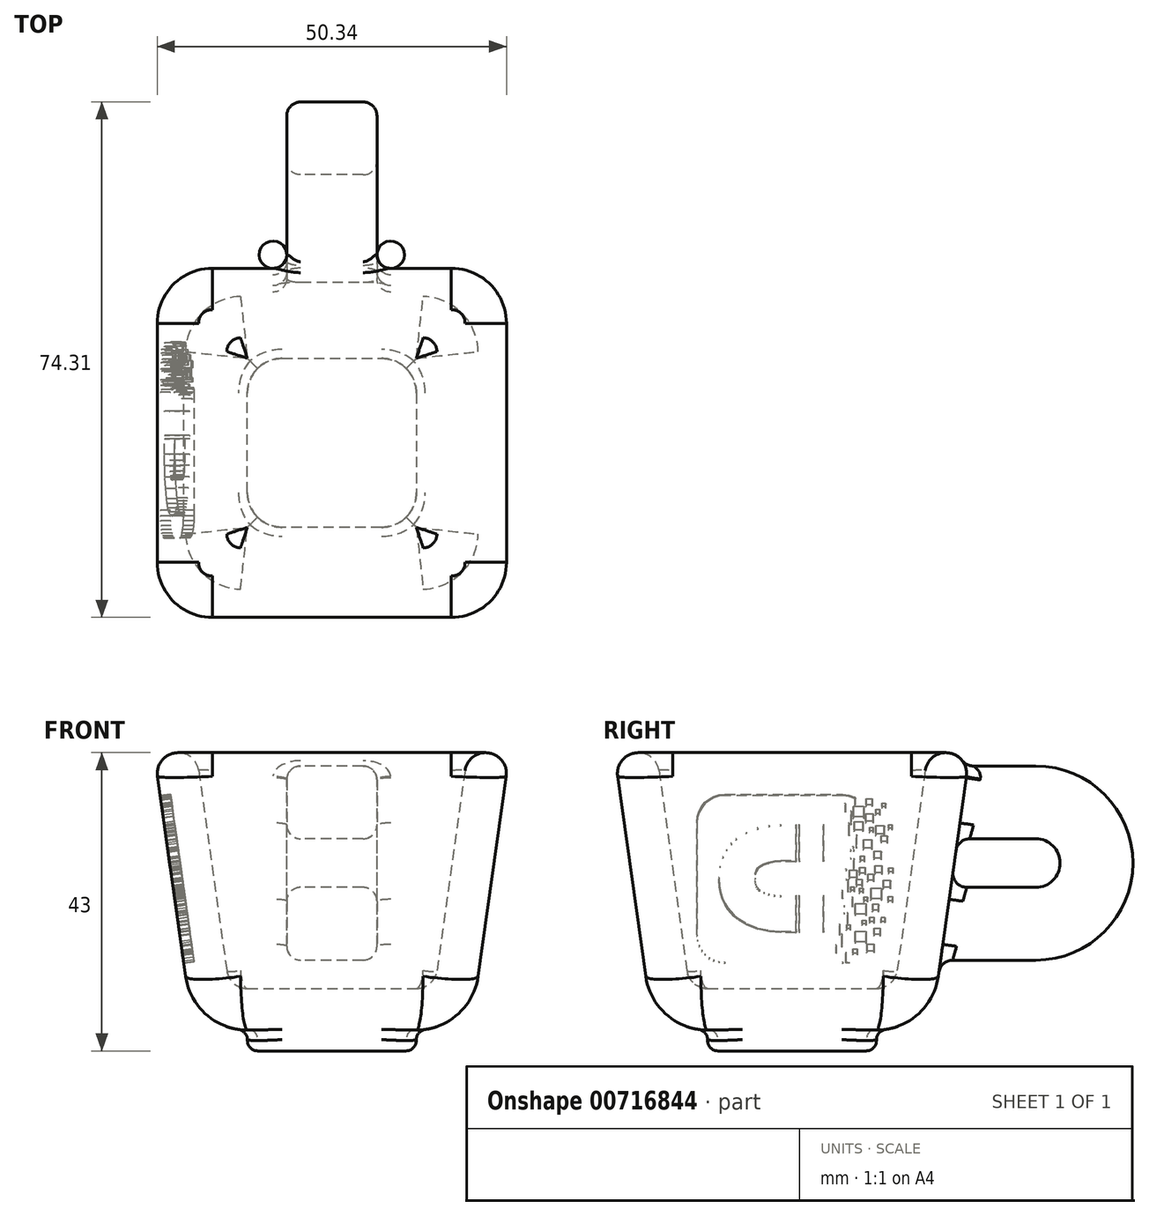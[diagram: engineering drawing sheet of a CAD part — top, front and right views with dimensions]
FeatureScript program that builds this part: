
annotation { "Feature Type Name" : "Feature", "Feature Type Description" : "" }
export const myFeature = defineFeature(function(context is Context, id is Id, definition is map)
    precondition{}
    {
        {
            var Q0;
            Q0=qCreatedBy(makeId("Top.planeOp"),FACE);
            var sketch = newSketch(context, id + "F0", { "sketchPlane" : qUnion([Q0])});
            skLineSegment(sketch, "E0.bottom", {"start": v(20, 20) * mm, "end": v(-20, 20) * mm});
            skLineSegment(sketch, "E0.top", {"start": v(20, -20) * mm, "end": v(-20, -20) * mm});
            skLineSegment(sketch, "E0.left", {"start": v(20, 20) * mm, "end": v(20, -20) * mm});
            skLineSegment(sketch, "E0.right", {"start": v(-20, 20) * mm, "end": v(-20, -20) * mm});
            skSolve(sketch);
        }
        {
            var Q0;
            Q0=makeQuery(id+"F0.imprint","IMPRINT",FACE,{"disambiguationData":[TD([[makeQuery(id+"F0.imprint","IMPRINT",EDGE,{"derivedFrom":sQuery(id+"F0.wireOp",EDGE,"E0.bottom")}),1.0]])]});
            extrude(context, id + "F1", {"entities" : qUnion([Q0]), "depth" : 40 * mm, "offsetDistance" : 25 * mm, "hasDraft" : true, "draftAngle" : 8 * degree});
        }
        {
            var Q0;
            Q0=makeQuery(id+"F1.opExtrude","SWEPT_EDGE",EDGE,{"disambiguationData":[OSD([sQuery(id+"F0.wireOp",EDGE,"E0.top"),sQuery(id+"F0.wireOp",EDGE,"E0.left")])]});
            var Q1;
            Q1=makeQuery(id+"F1.opExtrude","SWEPT_EDGE",EDGE,{"disambiguationData":[OSD([sQuery(id+"F0.wireOp",EDGE,"E0.top"),sQuery(id+"F0.wireOp",EDGE,"E0.right")])]});
            var Q2;
            Q2=makeQuery(id+"F1.opExtrude","SWEPT_EDGE",EDGE,{"disambiguationData":[OSD([sQuery(id+"F0.wireOp",EDGE,"E0.bottom"),sQuery(id+"F0.wireOp",EDGE,"E0.left")])]});
            var Q3;
            Q3=makeQuery(id+"F1.opExtrude","SWEPT_EDGE",EDGE,{"disambiguationData":[OSD([sQuery(id+"F0.wireOp",EDGE,"E0.bottom"),sQuery(id+"F0.wireOp",EDGE,"E0.right")])]});
            fillet(context, id + "F2", {"entities" : qUnion([Q0, Q1, Q2, Q3]), "radius" : 8 * mm, "tangentPropagation" : true, "allowEdgeOverflow" : false});
        }
        {
            var Q0;
            {var subQ0=sQuery(id+"F0.wireOp",EDGE,"E0.right");var subQ1=sQuery(id+"F0.wireOp",EDGE,"E0.bottom");Q0=makeQuery(id+"F2.opFillet","BLEND_EDGE",EDGE,{"blendedFrom":[makeQuery(id+"F1.opExtrude","SWEPT_EDGE",EDGE,{"disambiguationData":[OSD([subQ1,subQ0])]}),makeQuery(id+"F1.opExtrude","CAP_FACE",FACE,{"disambiguationData":[OSD([subQ1,sQuery(id+"F0.wireOp",EDGE,"E0.top"),sQuery(id+"F0.wireOp",EDGE,"E0.left"),subQ0])],"isStart":true})],"blendedInto":[makeQuery(id+"F1.opExtrude","CAP_FACE",FACE,{"disambiguationData":[OSD([subQ1,sQuery(id+"F0.wireOp",EDGE,"E0.top"),sQuery(id+"F0.wireOp",EDGE,"E0.left"),subQ0])],"isStart":true})]});}
            fillet(context, id + "F3", {"entities" : qUnion([Q0]), "radius" : 9 * mm, "tangentPropagation" : true, "allowEdgeOverflow" : false});
        }
        {
            var Q0;
            Q0=makeQuery(id+"F1.opExtrude","CAP_FACE",FACE,{"disambiguationData":[OSD([sQuery(id+"F0.wireOp",EDGE,"E0.bottom"),sQuery(id+"F0.wireOp",EDGE,"E0.top"),sQuery(id+"F0.wireOp",EDGE,"E0.left"),sQuery(id+"F0.wireOp",EDGE,"E0.right")])],"isStart":false});
            shell(context, id + "F4", {"entities" : qUnion([Q0]), "thickness" : 6 * mm});
        }
        {
            var Q0;
            {var subQ0=sQuery(id+"F0.wireOp",EDGE,"E0.left");Q0=makeQuery(id+"F4.opShell","OFFSET_EDGE",EDGE,{"disambiguationData":[OSD([subQ0]),TDD([makeQuery(id+"F1.opExtrude","CAP_EDGE",EDGE,{"disambiguationData":[OSD([subQ0])],"isStart":false})])]});}
            var Q1;
            {var subQ0=sQuery(id+"F0.wireOp",EDGE,"E0.left");var subQ1=sQuery(id+"F0.wireOp",EDGE,"E0.bottom");Q1=makeQuery(id+"F2.opFillet","BLEND_EDGE",EDGE,{"blendedFrom":[makeQuery(id+"F1.opExtrude","SWEPT_EDGE",EDGE,{"disambiguationData":[OSD([subQ1,subQ0])]}),makeQuery(id+"F1.opExtrude","CAP_FACE",FACE,{"disambiguationData":[OSD([subQ1,sQuery(id+"F0.wireOp",EDGE,"E0.top"),subQ0,sQuery(id+"F0.wireOp",EDGE,"E0.right")])],"isStart":false})],"blendedInto":[makeQuery(id+"F1.opExtrude","CAP_FACE",FACE,{"disambiguationData":[OSD([subQ1,sQuery(id+"F0.wireOp",EDGE,"E0.top"),subQ0,sQuery(id+"F0.wireOp",EDGE,"E0.right")])],"isStart":false})]});}
            fillet(context, id + "F5", {"entities" : qUnion([Q0, Q1]), "radius" : 3 * mm, "tangentPropagation" : true, "allowEdgeOverflow" : false});
        }
        {
            var Q0;
            Q0=qCreatedBy(makeId("Right.planeOp"),FACE);
            var sketch = newSketch(context, id + "F6", { "sketchPlane" : qUnion([Q0])});
            skArc(sketch, "E1", {"start": v(35.14, 20.58) * mm, "mid": v(38.64, 24.08) * mm, "end": v(35.14, 27.58) * mm});
            skLineSegment(sketch, "E2", {"start": v(35.14, 20.58) * mm, "end": v(20.07, 20.58) * mm});
            skLineSegment(sketch, "E3", {"start": v(35.14, 27.58) * mm, "end": v(20.46, 27.58) * mm});
            skLineSegment(sketch, "E4", {"start": v(35.14, 38.08) * mm, "end": v(21.04, 38.08) * mm});
            skLineSegment(sketch, "E5", {"start": v(35.14, 10.08) * mm, "end": v(18.28, 10.08) * mm});
            skLineSegment(sketch, "E6", {"start": v(18.28, 10.08) * mm, "end": v(20, 19.31) * mm});
            skLineSegment(sketch, "E7", {"start": v(20, 19.31) * mm, "end": v(20.07, 20.58) * mm});
            skLineSegment(sketch, "E8.trimOffspring", {"start": v(20.46, 27.58) * mm, "end": v(21.04, 38.08) * mm});
            skArc(sketch, "E9.trimOffspring", {"start": v(35.14, 10.08) * mm, "mid": v(49.14, 24.08) * mm, "end": v(35.14, 38.08) * mm});
            skPoint(sketch, "E10.0.start.orphan", {"position": v(25.14, 36.58) * mm});
            skPoint(sketch, "E11.trimOffspring.end.orphan", {"position": v(21.09, 7.75) * mm});
            skSolve(sketch);
        }
        {
            var Q0;
            Q0=makeQuery(id+"F6.imprint","IMPRINT",FACE,{"disambiguationData":[TD([[makeQuery(id+"F6.imprint","IMPRINT",EDGE,{"derivedFrom":sQuery(id+"F6.wireOp",EDGE,"E1")}),-1.0]])]});
            extrude(context, id + "F7", {"entities" : qUnion([Q0]), "operationType" : NewBodyOperationType.ADD, "depth" : 13 * mm, "offsetDistance" : 25 * mm, "symmetric" : true});
        }
        {
            var Q0;
            Q0=makeQuery(id+"F7.opExtrude","CAP_EDGE",EDGE,{"disambiguationData":[OSD([sQuery(id+"F6.wireOp",EDGE,"E9.trimOffspring")])],"isStart":false});
            var Q1;
            Q1=makeQuery(id+"F7.opExtrude","CAP_EDGE",EDGE,{"disambiguationData":[OSD([sQuery(id+"F6.wireOp",EDGE,"E3")])],"isStart":false});
            var Q2;
            Q2=makeQuery(id+"F7.opExtrude","CAP_EDGE",EDGE,{"disambiguationData":[OSD([sQuery(id+"F6.wireOp",EDGE,"E9.trimOffspring")])],"isStart":true});
            var Q3;
            Q3=makeQuery(id+"F7.opExtrude","CAP_EDGE",EDGE,{"disambiguationData":[OSD([sQuery(id+"F6.wireOp",EDGE,"E2")])],"isStart":true});
            fillet(context, id + "F8", {"entities" : qUnion([Q0, Q1, Q2, Q3]), "radius" : 2 * mm, "tangentPropagation" : true, "allowEdgeOverflow" : false});
        }
        {
            var Q0;
            Q0=makeQuery(id+"F8.opFillet","BLEND_EDGE",EDGE,{"blendedFrom":[makeQuery(id+"F7.opExtrude","CAP_EDGE",EDGE,{"disambiguationData":[OSD([sQuery(id+"F6.wireOp",EDGE,"E4")])],"isStart":true}),makeQuery(id+"F5.opFillet","BLEND_FACE",FACE,{"disambiguationData":[OSD([sQuery(id+"F0.wireOp",EDGE,"E0.bottom")])]})],"blendedInto":[makeQuery(id+"F5.opFillet","BLEND_FACE",FACE,{"disambiguationData":[OSD([sQuery(id+"F0.wireOp",EDGE,"E0.bottom")])]})]});
            var Q1;
            Q1=makeQuery(id+"F8.opFillet","BLEND_EDGE",EDGE,{"blendedFrom":[makeQuery(id+"F7.opExtrude","CAP_EDGE",EDGE,{"disambiguationData":[OSD([sQuery(id+"F6.wireOp",EDGE,"E2")])],"isStart":true}),makeQuery(id+"F1.opExtrude","SWEPT_FACE",FACE,{"disambiguationData":[OSD([sQuery(id+"F0.wireOp",EDGE,"E0.bottom")])]})],"blendedInto":[makeQuery(id+"F1.opExtrude","SWEPT_FACE",FACE,{"disambiguationData":[OSD([sQuery(id+"F0.wireOp",EDGE,"E0.bottom")])]})]});
            fillet(context, id + "F9", {"entities" : qUnion([Q0, Q1]), "radius" : 2 * mm, "tangentPropagation" : true, "allowEdgeOverflow" : false});
        }
        {
            var Q0;
            Q0=makeQuery(id+"F1.opExtrude","SWEPT_FACE",FACE,{"disambiguationData":[OSD([sQuery(id+"F0.wireOp",EDGE,"E0.right")])]});
            var sketch = newSketch(context, id + "F10", { "sketchPlane" : qUnion([Q0])});
            skLineSegment(sketch, "E12", {"start": v(-12.87, 18.96) * mm, "end": v(-12.87, 18.44) * mm});
            skLineSegment(sketch, "E13", {"start": v(-12.87, 18.44) * mm, "end": v(-13.38, 18.44) * mm});
            skLineSegment(sketch, "E14", {"start": v(-13.38, 18.44) * mm, "end": v(-13.38, 18.96) * mm});
            skLineSegment(sketch, "E15", {"start": v(-13.38, 18.96) * mm, "end": v(-12.87, 18.96) * mm});
            skLineSegment(sketch, "E16", {"start": v(-8.79, 13.79) * mm, "end": v(-8.79, 14.4) * mm});
            skLineSegment(sketch, "E17", {"start": v(-8.79, 14.4) * mm, "end": v(-9.4, 14.4) * mm});
            skLineSegment(sketch, "E18", {"start": v(-9.4, 14.4) * mm, "end": v(-9.4, 13.79) * mm});
            skLineSegment(sketch, "E19", {"start": v(-9.4, 13.79) * mm, "end": v(-8.79, 13.79) * mm});
            skLineSegment(sketch, "E20", {"start": v(-10.8, 14.1) * mm, "end": v(-10.8, 15.13) * mm});
            skLineSegment(sketch, "E21", {"start": v(-10.8, 15.13) * mm, "end": v(-11.83, 15.13) * mm});
            skLineSegment(sketch, "E22", {"start": v(-11.83, 15.13) * mm, "end": v(-11.83, 14.1) * mm});
            skLineSegment(sketch, "E23", {"start": v(-11.83, 14.1) * mm, "end": v(-10.8, 14.1) * mm});
            skLineSegment(sketch, "E24", {"start": v(-10.14, 18.04) * mm, "end": v(-10.14, 18.56) * mm});
            skLineSegment(sketch, "E25", {"start": v(-10.14, 18.56) * mm, "end": v(-10.65, 18.56) * mm});
            skLineSegment(sketch, "E26", {"start": v(-10.65, 18.56) * mm, "end": v(-10.65, 18.04) * mm});
            skLineSegment(sketch, "E27", {"start": v(-10.65, 18.04) * mm, "end": v(-10.14, 18.04) * mm});
            skLineSegment(sketch, "E28", {"start": v(-9.1, 15.4) * mm, "end": v(-9.1, 16.95) * mm});
            skLineSegment(sketch, "E29", {"start": v(-9.1, 16.95) * mm, "end": v(-10.65, 16.95) * mm});
            skLineSegment(sketch, "E30", {"start": v(-10.65, 16.95) * mm, "end": v(-10.65, 15.4) * mm});
            skLineSegment(sketch, "E31", {"start": v(-10.65, 15.4) * mm, "end": v(-9.1, 15.4) * mm});
            skLineSegment(sketch, "E32", {"start": v(-9.1, 19.44) * mm, "end": v(-9.1, 20.99) * mm});
            skLineSegment(sketch, "E33", {"start": v(-9.1, 20.99) * mm, "end": v(-10.65, 20.99) * mm});
            skLineSegment(sketch, "E34", {"start": v(-10.65, 20.99) * mm, "end": v(-10.65, 19.44) * mm});
            skLineSegment(sketch, "E35", {"start": v(-10.65, 19.44) * mm, "end": v(-9.1, 19.44) * mm});
            skLineSegment(sketch, "E36", {"start": v(-11.83, 16.5) * mm, "end": v(-11.83, 17.38) * mm});
            skLineSegment(sketch, "E37", {"start": v(-11.83, 17.38) * mm, "end": v(-12.72, 17.38) * mm});
            skLineSegment(sketch, "E38", {"start": v(-12.72, 17.38) * mm, "end": v(-12.72, 16.5) * mm});
            skLineSegment(sketch, "E39", {"start": v(-12.72, 16.5) * mm, "end": v(-11.83, 16.5) * mm});
            skLineSegment(sketch, "E40", {"start": v(-11.6, 20.02) * mm, "end": v(-11.6, 20.9) * mm});
            skLineSegment(sketch, "E41", {"start": v(-11.6, 20.9) * mm, "end": v(-12.48, 20.9) * mm});
            skLineSegment(sketch, "E42", {"start": v(-12.48, 20.9) * mm, "end": v(-12.48, 20.02) * mm});
            skLineSegment(sketch, "E43", {"start": v(-12.48, 20.02) * mm, "end": v(-11.6, 20.02) * mm});
            skLineSegment(sketch, "E44", {"start": v(-8.46, 23.47) * mm, "end": v(-8.97, 23.47) * mm});
            skLineSegment(sketch, "E45", {"start": v(-8.97, 23.47) * mm, "end": v(-8.97, 22.95) * mm});
            skLineSegment(sketch, "E46", {"start": v(-8.97, 22.95) * mm, "end": v(-8.46, 22.95) * mm});
            skLineSegment(sketch, "E47", {"start": v(-8.46, 22.95) * mm, "end": v(-8.46, 23.47) * mm});
            skLineSegment(sketch, "E48", {"start": v(-9.29, 24.5) * mm, "end": v(-10.12, 24.5) * mm});
            skLineSegment(sketch, "E49", {"start": v(-10.12, 24.5) * mm, "end": v(-10.12, 23.67) * mm});
            skLineSegment(sketch, "E50", {"start": v(-10.12, 23.67) * mm, "end": v(-9.29, 23.67) * mm});
            skLineSegment(sketch, "E51", {"start": v(-9.29, 23.67) * mm, "end": v(-9.29, 24.5) * mm});
            skLineSegment(sketch, "E52", {"start": v(-9.74, 26.26) * mm, "end": v(-10.57, 26.26) * mm});
            skLineSegment(sketch, "E53", {"start": v(-10.57, 26.26) * mm, "end": v(-10.57, 25.43) * mm});
            skLineSegment(sketch, "E54", {"start": v(-10.57, 25.43) * mm, "end": v(-9.74, 25.43) * mm});
            skLineSegment(sketch, "E55", {"start": v(-9.74, 25.43) * mm, "end": v(-9.74, 26.26) * mm});
            skLineSegment(sketch, "E56", {"start": v(-14.5, 21.39) * mm, "end": v(-13.88, 21.39) * mm});
            skLineSegment(sketch, "E57", {"start": v(-13.88, 21.39) * mm, "end": v(-13.88, 22) * mm});
            skLineSegment(sketch, "E58", {"start": v(-13.88, 22) * mm, "end": v(-14.5, 22) * mm});
            skLineSegment(sketch, "E59", {"start": v(-14.5, 22) * mm, "end": v(-14.5, 21.39) * mm});
            skLineSegment(sketch, "E60", {"start": v(-11.82, 18.38) * mm, "end": v(-11.2, 18.38) * mm});
            skLineSegment(sketch, "E61", {"start": v(-11.2, 18.38) * mm, "end": v(-11.2, 19) * mm});
            skLineSegment(sketch, "E62", {"start": v(-11.2, 19) * mm, "end": v(-11.82, 19) * mm});
            skLineSegment(sketch, "E63", {"start": v(-11.82, 19) * mm, "end": v(-11.82, 18.38) * mm});
            skLineSegment(sketch, "E64", {"start": v(-14.53, 25.6) * mm, "end": v(-13.91, 25.6) * mm});
            skLineSegment(sketch, "E65", {"start": v(-13.91, 25.6) * mm, "end": v(-13.91, 26.21) * mm});
            skLineSegment(sketch, "E66", {"start": v(-13.91, 26.21) * mm, "end": v(-14.53, 26.21) * mm});
            skLineSegment(sketch, "E67", {"start": v(-14.53, 26.21) * mm, "end": v(-14.53, 25.6) * mm});
            skLineSegment(sketch, "E68", {"start": v(-14.2, 23.38) * mm, "end": v(-13.16, 23.38) * mm});
            skLineSegment(sketch, "E69", {"start": v(-13.16, 23.38) * mm, "end": v(-13.16, 24.41) * mm});
            skLineSegment(sketch, "E70", {"start": v(-13.16, 24.41) * mm, "end": v(-14.2, 24.41) * mm});
            skLineSegment(sketch, "E71", {"start": v(-14.2, 24.41) * mm, "end": v(-14.2, 23.38) * mm});
            skLineSegment(sketch, "E72", {"start": v(-12.98, 25.48) * mm, "end": v(-11.95, 25.48) * mm});
            skLineSegment(sketch, "E73", {"start": v(-11.95, 25.48) * mm, "end": v(-11.95, 26.51) * mm});
            skLineSegment(sketch, "E74", {"start": v(-11.95, 26.51) * mm, "end": v(-12.98, 26.51) * mm});
            skLineSegment(sketch, "E75", {"start": v(-12.98, 26.51) * mm, "end": v(-12.98, 25.48) * mm});
            skLineSegment(sketch, "E76", {"start": v(-10.25, 22.73) * mm, "end": v(-9.74, 22.73) * mm});
            skLineSegment(sketch, "E77", {"start": v(-9.74, 22.73) * mm, "end": v(-9.74, 23.25) * mm});
            skLineSegment(sketch, "E78", {"start": v(-9.74, 23.25) * mm, "end": v(-10.25, 23.25) * mm});
            skLineSegment(sketch, "E79", {"start": v(-10.25, 23.25) * mm, "end": v(-10.25, 22.73) * mm});
            skLineSegment(sketch, "E80", {"start": v(-10.89, 21.45) * mm, "end": v(-10.37, 21.45) * mm});
            skLineSegment(sketch, "E81", {"start": v(-10.37, 21.45) * mm, "end": v(-10.37, 21.97) * mm});
            skLineSegment(sketch, "E82", {"start": v(-10.37, 21.97) * mm, "end": v(-10.89, 21.97) * mm});
            skLineSegment(sketch, "E83", {"start": v(-10.89, 21.97) * mm, "end": v(-10.89, 21.45) * mm});
            skLineSegment(sketch, "E84", {"start": v(-8.42, 17.34) * mm, "end": v(-7.86, 17.34) * mm});
            skLineSegment(sketch, "E85", {"start": v(-7.86, 17.34) * mm, "end": v(-7.86, 17.91) * mm});
            skLineSegment(sketch, "E86", {"start": v(-7.86, 17.91) * mm, "end": v(-8.42, 17.91) * mm});
            skLineSegment(sketch, "E87", {"start": v(-8.42, 17.91) * mm, "end": v(-8.42, 17.34) * mm});
            skLineSegment(sketch, "E88", {"start": v(-12.9, 21.7) * mm, "end": v(-11.35, 21.7) * mm});
            skLineSegment(sketch, "E89", {"start": v(-11.35, 21.7) * mm, "end": v(-11.35, 23.25) * mm});
            skLineSegment(sketch, "E90", {"start": v(-11.35, 23.25) * mm, "end": v(-12.9, 23.25) * mm});
            skLineSegment(sketch, "E91", {"start": v(-12.9, 23.25) * mm, "end": v(-12.9, 21.7) * mm});
            skLineSegment(sketch, "E92", {"start": v(-9.36, 24.78) * mm, "end": v(-8.24, 24.78) * mm});
            skLineSegment(sketch, "E93", {"start": v(-8.24, 24.78) * mm, "end": v(-8.24, 25.9) * mm});
            skLineSegment(sketch, "E94", {"start": v(-8.24, 25.9) * mm, "end": v(-9.36, 25.9) * mm});
            skLineSegment(sketch, "E95", {"start": v(-9.36, 25.9) * mm, "end": v(-9.36, 24.78) * mm});
            skLineSegment(sketch, "E96", {"start": v(-11.78, 24.41) * mm, "end": v(-10.9, 24.41) * mm});
            skLineSegment(sketch, "E97", {"start": v(-10.9, 24.41) * mm, "end": v(-10.9, 25.3) * mm});
            skLineSegment(sketch, "E98", {"start": v(-10.9, 25.3) * mm, "end": v(-11.78, 25.3) * mm});
            skLineSegment(sketch, "E99", {"start": v(-11.78, 25.3) * mm, "end": v(-11.78, 24.41) * mm});
            skLineSegment(sketch, "E100", {"start": v(-11.55, 35.36) * mm, "end": v(-10.67, 35.36) * mm});
            skLineSegment(sketch, "E101", {"start": v(-10.67, 35.36) * mm, "end": v(-10.67, 36.24) * mm});
            skLineSegment(sketch, "E102", {"start": v(-10.67, 36.24) * mm, "end": v(-11.55, 36.24) * mm});
            skLineSegment(sketch, "E103", {"start": v(-11.55, 36.24) * mm, "end": v(-11.55, 35.36) * mm});
            skLineSegment(sketch, "E104", {"start": v(-14.43, 32.48) * mm, "end": v(-14.43, 31.97) * mm});
            skLineSegment(sketch, "E105", {"start": v(-14.43, 31.97) * mm, "end": v(-13.91, 31.97) * mm});
            skLineSegment(sketch, "E106", {"start": v(-13.91, 31.97) * mm, "end": v(-13.91, 32.48) * mm});
            skLineSegment(sketch, "E107", {"start": v(-13.91, 32.48) * mm, "end": v(-14.43, 32.48) * mm});
            skLineSegment(sketch, "E108", {"start": v(-13.48, 35.64) * mm, "end": v(-13.48, 35.13) * mm});
            skLineSegment(sketch, "E109", {"start": v(-13.48, 35.13) * mm, "end": v(-12.96, 35.13) * mm});
            skLineSegment(sketch, "E110", {"start": v(-12.96, 35.13) * mm, "end": v(-12.96, 35.64) * mm});
            skLineSegment(sketch, "E111", {"start": v(-12.96, 35.64) * mm, "end": v(-13.48, 35.64) * mm});
            skLineSegment(sketch, "E112", {"start": v(-9.84, 27.3) * mm, "end": v(-9.84, 27.92) * mm});
            skLineSegment(sketch, "E113", {"start": v(-9.84, 27.92) * mm, "end": v(-10.45, 27.92) * mm});
            skLineSegment(sketch, "E114", {"start": v(-10.45, 27.92) * mm, "end": v(-10.45, 27.3) * mm});
            skLineSegment(sketch, "E115", {"start": v(-10.45, 27.3) * mm, "end": v(-9.84, 27.3) * mm});
            skLineSegment(sketch, "E116", {"start": v(-11.83, 27.62) * mm, "end": v(-11.83, 28.66) * mm});
            skLineSegment(sketch, "E117", {"start": v(-11.83, 28.66) * mm, "end": v(-12.87, 28.66) * mm});
            skLineSegment(sketch, "E118", {"start": v(-12.87, 28.66) * mm, "end": v(-12.87, 27.62) * mm});
            skLineSegment(sketch, "E119", {"start": v(-12.87, 27.62) * mm, "end": v(-11.83, 27.62) * mm});
            skLineSegment(sketch, "E120", {"start": v(-11.17, 31.57) * mm, "end": v(-11.17, 32.08) * mm});
            skLineSegment(sketch, "E121", {"start": v(-11.17, 32.08) * mm, "end": v(-11.68, 32.08) * mm});
            skLineSegment(sketch, "E122", {"start": v(-11.68, 32.08) * mm, "end": v(-11.68, 31.57) * mm});
            skLineSegment(sketch, "E123", {"start": v(-11.68, 31.57) * mm, "end": v(-11.17, 31.57) * mm});
            skLineSegment(sketch, "E124", {"start": v(-10.3, 29.09) * mm, "end": v(-10.3, 30.3) * mm});
            skLineSegment(sketch, "E125", {"start": v(-10.3, 30.3) * mm, "end": v(-11.52, 30.3) * mm});
            skLineSegment(sketch, "E126", {"start": v(-11.52, 30.3) * mm, "end": v(-11.52, 29.09) * mm});
            skLineSegment(sketch, "E127", {"start": v(-11.52, 29.09) * mm, "end": v(-10.3, 29.09) * mm});
            skLineSegment(sketch, "E128", {"start": v(-12.08, 31.15) * mm, "end": v(-12.08, 32.37) * mm});
            skLineSegment(sketch, "E129", {"start": v(-12.08, 32.37) * mm, "end": v(-13.3, 32.37) * mm});
            skLineSegment(sketch, "E130", {"start": v(-13.3, 32.37) * mm, "end": v(-13.3, 31.15) * mm});
            skLineSegment(sketch, "E131", {"start": v(-13.3, 31.15) * mm, "end": v(-12.08, 31.15) * mm});
            skLineSegment(sketch, "E132", {"start": v(-12.05, 34.11) * mm, "end": v(-12.05, 34.71) * mm});
            skLineSegment(sketch, "E133", {"start": v(-12.05, 34.71) * mm, "end": v(-12.65, 34.71) * mm});
            skLineSegment(sketch, "E134", {"start": v(-12.65, 34.71) * mm, "end": v(-12.65, 34.11) * mm});
            skLineSegment(sketch, "E135", {"start": v(-12.65, 34.11) * mm, "end": v(-12.05, 34.11) * mm});
            skLineSegment(sketch, "E136", {"start": v(-8.99, 31.72) * mm, "end": v(-8.99, 32.93) * mm});
            skLineSegment(sketch, "E137", {"start": v(-8.99, 32.93) * mm, "end": v(-10.2, 32.93) * mm});
            skLineSegment(sketch, "E138", {"start": v(-10.2, 32.93) * mm, "end": v(-10.2, 31.72) * mm});
            skLineSegment(sketch, "E139", {"start": v(-10.2, 31.72) * mm, "end": v(-8.99, 31.72) * mm});
            skLineSegment(sketch, "E140", {"start": v(-10.59, 32.96) * mm, "end": v(-10.59, 34.06) * mm});
            skLineSegment(sketch, "E141", {"start": v(-10.59, 34.06) * mm, "end": v(-11.68, 34.06) * mm});
            skLineSegment(sketch, "E142", {"start": v(-11.68, 34.06) * mm, "end": v(-11.68, 32.96) * mm});
            skLineSegment(sketch, "E143", {"start": v(-11.68, 32.96) * mm, "end": v(-10.59, 32.96) * mm});
            skLineSegment(sketch, "E144", {"start": v(-8.82, 33.61) * mm, "end": v(-8.82, 35.16) * mm});
            skLineSegment(sketch, "E145", {"start": v(-8.82, 35.16) * mm, "end": v(-10.37, 35.16) * mm});
            skLineSegment(sketch, "E146", {"start": v(-10.37, 35.16) * mm, "end": v(-10.37, 33.61) * mm});
            skLineSegment(sketch, "E147", {"start": v(-10.37, 33.61) * mm, "end": v(-8.82, 33.61) * mm});
            skLineSegment(sketch, "E148", {"start": v(-12.87, 30.02) * mm, "end": v(-12.87, 30.9) * mm});
            skLineSegment(sketch, "E149", {"start": v(-12.87, 30.9) * mm, "end": v(-13.75, 30.9) * mm});
            skLineSegment(sketch, "E150", {"start": v(-13.75, 30.9) * mm, "end": v(-13.75, 30.02) * mm});
            skLineSegment(sketch, "E151", {"start": v(-13.75, 30.02) * mm, "end": v(-12.87, 30.02) * mm});
            skLineSegment(sketch, "E152", {"start": v(-9.09, 35.56) * mm, "end": v(-7.68, 35.56) * mm});
            skLineSegment(sketch, "E153", {"start": v(-7.68, 35.56) * mm, "end": v(-7.68, 34.48) * mm});
            skLineSegment(sketch, "E154", {"start": v(-7.68, 34.48) * mm, "end": v(-8.5, 34.48) * mm});
            skLineSegment(sketch, "E155", {"start": v(-8.5, 34.48) * mm, "end": v(-8.5, 32.66) * mm});
            skLineSegment(sketch, "E156", {"start": v(-8.5, 32.66) * mm, "end": v(-8.2, 32.66) * mm});
            skLineSegment(sketch, "E157", {"start": v(-8.2, 32.66) * mm, "end": v(-8.2, 31.08) * mm});
            skLineSegment(sketch, "E158", {"start": v(-8.2, 31.08) * mm, "end": v(-9.3, 31.08) * mm});
            skLineSegment(sketch, "E159", {"start": v(-9.3, 31.08) * mm, "end": v(-9.3, 29.27) * mm});
            skLineSegment(sketch, "E160", {"start": v(-9.3, 29.27) * mm, "end": v(-8.82, 29.27) * mm});
            skLineSegment(sketch, "E161", {"start": v(-8.82, 29.27) * mm, "end": v(-8.9, 28.82) * mm});
            skLineSegment(sketch, "E162", {"start": v(-8.9, 28.82) * mm, "end": v(-8.46, 28.8) * mm});
            skLineSegment(sketch, "E163", {"start": v(-8.46, 28.8) * mm, "end": v(-8.44, 27.64) * mm});
            skLineSegment(sketch, "E164", {"start": v(-8.44, 27.64) * mm, "end": v(-8.92, 27.64) * mm});
            skLineSegment(sketch, "E165", {"start": v(-8.92, 27.64) * mm, "end": v(-8.92, 26) * mm});
            skLineSegment(sketch, "E166", {"start": v(-8.92, 26) * mm, "end": v(-7.83, 26) * mm});
            skLineSegment(sketch, "E167", {"start": v(-7.83, 26) * mm, "end": v(-7.8, 24.56) * mm});
            skLineSegment(sketch, "E168", {"start": v(-7.8, 24.56) * mm, "end": v(-8.1, 24.56) * mm});
            skLineSegment(sketch, "E169", {"start": v(-8.1, 24.56) * mm, "end": v(-8.1, 22.92) * mm});
            skLineSegment(sketch, "E170", {"start": v(-8.1, 22.92) * mm, "end": v(-7.28, 22.92) * mm});
            skLineSegment(sketch, "E171", {"start": v(-7.28, 22.92) * mm, "end": v(-7.28, 21.94) * mm});
            skLineSegment(sketch, "E172", {"start": v(-7.28, 21.94) * mm, "end": v(-8.7, 21.94) * mm});
            skLineSegment(sketch, "E173", {"start": v(-8.7, 21.94) * mm, "end": v(-8.7, 20.72) * mm});
            skLineSegment(sketch, "E174", {"start": v(-8.7, 20.72) * mm, "end": v(-7.53, 20.72) * mm});
            skLineSegment(sketch, "E175", {"start": v(-7.53, 20.72) * mm, "end": v(-7.5, 19.66) * mm});
            skLineSegment(sketch, "E176", {"start": v(-7.5, 19.66) * mm, "end": v(-8, 19.66) * mm});
            skLineSegment(sketch, "E177", {"start": v(-8, 19.66) * mm, "end": v(-8, 18.01) * mm});
            skLineSegment(sketch, "E178", {"start": v(-8, 18.01) * mm, "end": v(-6.9, 18.01) * mm});
            skLineSegment(sketch, "E179", {"start": v(-6.9, 18.01) * mm, "end": v(-6.9, 16.58) * mm});
            skLineSegment(sketch, "E180", {"start": v(-6.9, 16.58) * mm, "end": v(-7.18, 16.58) * mm});
            skLineSegment(sketch, "E181", {"start": v(-7.18, 16.58) * mm, "end": v(-7.18, 14.93) * mm});
            skLineSegment(sketch, "E182", {"start": v(-7.18, 14.93) * mm, "end": v(-6.36, 14.93) * mm});
            skLineSegment(sketch, "E183", {"start": v(-6.36, 14.93) * mm, "end": v(-6.36, 13.95) * mm});
            skLineSegment(sketch, "E184", {"start": v(-6.36, 13.95) * mm, "end": v(-7.78, 13.95) * mm});
            skLineSegment(sketch, "E185", {"start": v(-7.78, 13.95) * mm, "end": v(-7.78, 12.55) * mm});
            skLineSegment(sketch, "E186", {"start": v(-7.78, 12.55) * mm, "end": v(-7.9, 12.54) * mm});
            skLineSegment(sketch, "E187", {"start": v(-7.9, 12.54) * mm, "end": v(-7.3, 12.49) * mm});
            skLineSegment(sketch, "E188", {"start": v(-7.3, 12.49) * mm, "end": v(9.7, 12.49) * mm});
            skLineSegment(sketch, "E189", {"start": v(9.7, 12.49) * mm, "end": v(10.51, 12.57) * mm});
            skLineSegment(sketch, "E190", {"start": v(10.51, 12.57) * mm, "end": v(11.26, 12.8) * mm});
            skLineSegment(sketch, "E191", {"start": v(11.26, 12.8) * mm, "end": v(11.94, 13.17) * mm});
            skLineSegment(sketch, "E192", {"start": v(11.94, 13.17) * mm, "end": v(12.53, 13.65) * mm});
            skLineSegment(sketch, "E193", {"start": v(12.53, 13.65) * mm, "end": v(13.02, 14.24) * mm});
            skLineSegment(sketch, "E194", {"start": v(13.02, 14.24) * mm, "end": v(13.39, 14.92) * mm});
            skLineSegment(sketch, "E195", {"start": v(13.39, 14.92) * mm, "end": v(13.62, 15.67) * mm});
            skLineSegment(sketch, "E196", {"start": v(13.62, 15.67) * mm, "end": v(13.7, 16.48) * mm});
            skLineSegment(sketch, "E197", {"start": v(13.7, 16.48) * mm, "end": v(13.7, 32.91) * mm});
            skLineSegment(sketch, "E198", {"start": v(13.7, 32.91) * mm, "end": v(13.62, 33.72) * mm});
            skLineSegment(sketch, "E199", {"start": v(13.62, 33.72) * mm, "end": v(13.39, 34.47) * mm});
            skLineSegment(sketch, "E200", {"start": v(13.39, 34.47) * mm, "end": v(13.02, 35.15) * mm});
            skLineSegment(sketch, "E201", {"start": v(13.02, 35.15) * mm, "end": v(12.53, 35.74) * mm});
            skLineSegment(sketch, "E202", {"start": v(12.53, 35.74) * mm, "end": v(11.94, 36.23) * mm});
            skLineSegment(sketch, "E203", {"start": v(11.94, 36.23) * mm, "end": v(11.26, 36.6) * mm});
            skLineSegment(sketch, "E204", {"start": v(11.26, 36.6) * mm, "end": v(10.51, 36.83) * mm});
            skLineSegment(sketch, "E205", {"start": v(10.51, 36.83) * mm, "end": v(9.7, 36.9) * mm});
            skLineSegment(sketch, "E206", {"start": v(9.7, 36.9) * mm, "end": v(-7.3, 36.9) * mm});
            skLineSegment(sketch, "E207", {"start": v(-7.3, 36.9) * mm, "end": v(-8.23, 36.8) * mm});
            skLineSegment(sketch, "E208", {"start": v(-8.23, 36.8) * mm, "end": v(-9.09, 36.47) * mm});
            skLineSegment(sketch, "E209", {"start": v(-9.09, 36.47) * mm, "end": v(-9.09, 35.56) * mm});
            skLineSegment(sketch, "E210", {"start": v(1.66, 32.48) * mm, "end": v(3.29, 32.34) * mm});
            skLineSegment(sketch, "E211", {"start": v(3.29, 32.34) * mm, "end": v(4.96, 31.99) * mm});
            skLineSegment(sketch, "E212", {"start": v(4.96, 31.99) * mm, "end": v(6.59, 31.37) * mm});
            skLineSegment(sketch, "E213", {"start": v(6.59, 31.37) * mm, "end": v(8.06, 30.42) * mm});
            skLineSegment(sketch, "E214", {"start": v(8.06, 30.42) * mm, "end": v(8.76, 29.76) * mm});
            skLineSegment(sketch, "E215", {"start": v(8.76, 29.76) * mm, "end": v(9.42, 28.89) * mm});
            skLineSegment(sketch, "E216", {"start": v(9.42, 28.89) * mm, "end": v(10, 27.79) * mm});
            skLineSegment(sketch, "E217", {"start": v(10, 27.79) * mm, "end": v(10.39, 26.44) * mm});
            skLineSegment(sketch, "E218", {"start": v(10.39, 26.44) * mm, "end": v(10.54, 24.8) * mm});
            skLineSegment(sketch, "E219", {"start": v(10.54, 24.8) * mm, "end": v(10.54, 24.66) * mm});
            skLineSegment(sketch, "E220", {"start": v(10.54, 24.66) * mm, "end": v(10.46, 23.6) * mm});
            skLineSegment(sketch, "E221", {"start": v(10.46, 23.6) * mm, "end": v(10.28, 22.64) * mm});
            skLineSegment(sketch, "E222", {"start": v(10.28, 22.64) * mm, "end": v(10, 21.79) * mm});
            skLineSegment(sketch, "E223", {"start": v(10, 21.79) * mm, "end": v(9.66, 21.04) * mm});
            skLineSegment(sketch, "E224", {"start": v(9.66, 21.04) * mm, "end": v(9.25, 20.39) * mm});
            skLineSegment(sketch, "E225", {"start": v(9.25, 20.39) * mm, "end": v(8.81, 19.83) * mm});
            skLineSegment(sketch, "E226", {"start": v(8.81, 19.83) * mm, "end": v(8.36, 19.35) * mm});
            skLineSegment(sketch, "E227", {"start": v(8.36, 19.35) * mm, "end": v(7.91, 18.96) * mm});
            skLineSegment(sketch, "E228", {"start": v(7.91, 18.96) * mm, "end": v(6.46, 18.04) * mm});
            skLineSegment(sketch, "E229", {"start": v(6.46, 18.04) * mm, "end": v(4.87, 17.44) * mm});
            skLineSegment(sketch, "E230", {"start": v(4.87, 17.44) * mm, "end": v(3.23, 17.1) * mm});
            skLineSegment(sketch, "E231", {"start": v(3.23, 17.1) * mm, "end": v(1.64, 16.96) * mm});
            skLineSegment(sketch, "E232", {"start": v(1.64, 16.96) * mm, "end": v(-0.59, 16.96) * mm});
            skLineSegment(sketch, "E233", {"start": v(-0.59, 16.96) * mm, "end": v(-0.59, 22.15) * mm});
            skLineSegment(sketch, "E234", {"start": v(-0.59, 22.15) * mm, "end": v(1.64, 22.15) * mm});
            skLineSegment(sketch, "E235", {"start": v(1.64, 22.15) * mm, "end": v(2.51, 22.24) * mm});
            skLineSegment(sketch, "E236", {"start": v(2.51, 22.24) * mm, "end": v(3.33, 22.4) * mm});
            skLineSegment(sketch, "E237", {"start": v(3.33, 22.4) * mm, "end": v(4.07, 22.65) * mm});
            skLineSegment(sketch, "E238", {"start": v(4.07, 22.65) * mm, "end": v(4.67, 23) * mm});
            skLineSegment(sketch, "E239", {"start": v(4.67, 23) * mm, "end": v(4.82, 23.14) * mm});
            skLineSegment(sketch, "E240", {"start": v(4.82, 23.14) * mm, "end": v(4.97, 23.32) * mm});
            skLineSegment(sketch, "E241", {"start": v(4.97, 23.32) * mm, "end": v(5.12, 23.55) * mm});
            skLineSegment(sketch, "E242", {"start": v(5.12, 23.55) * mm, "end": v(5.23, 23.85) * mm});
            skLineSegment(sketch, "E243", {"start": v(5.23, 23.85) * mm, "end": v(5.32, 24.24) * mm});
            skLineSegment(sketch, "E244", {"start": v(5.32, 24.24) * mm, "end": v(5.35, 24.73) * mm});
            skLineSegment(sketch, "E245", {"start": v(5.35, 24.73) * mm, "end": v(5.3, 25.4) * mm});
            skLineSegment(sketch, "E246", {"start": v(5.3, 25.4) * mm, "end": v(5.16, 25.87) * mm});
            skLineSegment(sketch, "E247", {"start": v(5.16, 25.87) * mm, "end": v(4.96, 26.2) * mm});
            skLineSegment(sketch, "E248", {"start": v(4.96, 26.2) * mm, "end": v(4.73, 26.41) * mm});
            skLineSegment(sketch, "E249", {"start": v(4.73, 26.41) * mm, "end": v(4.13, 26.78) * mm});
            skLineSegment(sketch, "E250", {"start": v(4.13, 26.78) * mm, "end": v(3.39, 27.04) * mm});
            skLineSegment(sketch, "E251", {"start": v(3.39, 27.04) * mm, "end": v(2.54, 27.2) * mm});
            skLineSegment(sketch, "E252", {"start": v(2.54, 27.2) * mm, "end": v(1.64, 27.28) * mm});
            skLineSegment(sketch, "E253", {"start": v(1.64, 27.28) * mm, "end": v(-0.59, 27.28) * mm});
            skLineSegment(sketch, "E254", {"start": v(-0.59, 27.28) * mm, "end": v(-0.59, 32.47) * mm});
            skLineSegment(sketch, "E255", {"start": v(-0.59, 32.47) * mm, "end": v(1.66, 32.48) * mm});
            skLineSegment(sketch, "E256", {"start": v(-4.55, 27.3) * mm, "end": v(-1.06, 27.3) * mm});
            skLineSegment(sketch, "E257", {"start": v(-1.06, 27.3) * mm, "end": v(-1.06, 32.48) * mm});
            skLineSegment(sketch, "E258", {"start": v(-1.06, 32.48) * mm, "end": v(-4.55, 32.48) * mm});
            skLineSegment(sketch, "E259", {"start": v(-4.55, 32.48) * mm, "end": v(-4.55, 27.3) * mm});
            skLineSegment(sketch, "E260", {"start": v(-4.55, 16.96) * mm, "end": v(-1.06, 16.96) * mm});
            skLineSegment(sketch, "E261", {"start": v(-1.06, 16.96) * mm, "end": v(-1.06, 22.15) * mm});
            skLineSegment(sketch, "E262", {"start": v(-1.06, 22.15) * mm, "end": v(-4.55, 22.15) * mm});
            skLineSegment(sketch, "E263", {"start": v(-4.55, 22.15) * mm, "end": v(-4.55, 16.96) * mm});
            skSolve(sketch);
        }
        {
            var Q0;
            Q0=makeQuery(id+"F10.imprint","IMPRINT",FACE,{"disambiguationData":[TD([[makeQuery(id+"F10.imprint","IMPRINT",EDGE,{"derivedFrom":sQuery(id+"F10.wireOp",EDGE,"E152")}),1.0]])]});
            var Q1;
            Q1=makeQuery(id+"F10.imprint","IMPRINT",FACE,{"disambiguationData":[TD([[makeQuery(id+"F10.imprint","IMPRINT",EDGE,{"derivedFrom":sQuery(id+"F10.wireOp",EDGE,"E144")}),1.0]])]});
            var Q2;
            Q2=makeQuery(id+"F10.imprint","IMPRINT",FACE,{"disambiguationData":[TD([[makeQuery(id+"F10.imprint","IMPRINT",EDGE,{"derivedFrom":sQuery(id+"F10.wireOp",EDGE,"E140")}),1.0]])]});
            var Q3;
            Q3=makeQuery(id+"F10.imprint","IMPRINT",FACE,{"disambiguationData":[TD([[makeQuery(id+"F10.imprint","IMPRINT",EDGE,{"derivedFrom":sQuery(id+"F10.wireOp",EDGE,"E100")}),1.0]])]});
            var Q4;
            Q4=makeQuery(id+"F10.imprint","IMPRINT",FACE,{"disambiguationData":[TD([[makeQuery(id+"F10.imprint","IMPRINT",EDGE,{"derivedFrom":sQuery(id+"F10.wireOp",EDGE,"E108")}),1.0]])]});
            var Q5;
            Q5=makeQuery(id+"F10.imprint","IMPRINT",FACE,{"disambiguationData":[TD([[makeQuery(id+"F10.imprint","IMPRINT",EDGE,{"derivedFrom":sQuery(id+"F10.wireOp",EDGE,"E128")}),1.0]])]});
            var Q6;
            Q6=makeQuery(id+"F10.imprint","IMPRINT",FACE,{"disambiguationData":[TD([[makeQuery(id+"F10.imprint","IMPRINT",EDGE,{"derivedFrom":sQuery(id+"F10.wireOp",EDGE,"E104")}),1.0]])]});
            var Q7;
            Q7=makeQuery(id+"F10.imprint","IMPRINT",FACE,{"disambiguationData":[TD([[makeQuery(id+"F10.imprint","IMPRINT",EDGE,{"derivedFrom":sQuery(id+"F10.wireOp",EDGE,"E120")}),1.0]])]});
            var Q8;
            Q8=makeQuery(id+"F10.imprint","IMPRINT",FACE,{"disambiguationData":[TD([[makeQuery(id+"F10.imprint","IMPRINT",EDGE,{"derivedFrom":sQuery(id+"F10.wireOp",EDGE,"E148")}),1.0]])]});
            var Q9;
            Q9=makeQuery(id+"F10.imprint","IMPRINT",FACE,{"disambiguationData":[TD([[makeQuery(id+"F10.imprint","IMPRINT",EDGE,{"derivedFrom":sQuery(id+"F10.wireOp",EDGE,"E116")}),1.0]])]});
            var Q10;
            Q10=makeQuery(id+"F10.imprint","IMPRINT",FACE,{"disambiguationData":[TD([[makeQuery(id+"F10.imprint","IMPRINT",EDGE,{"derivedFrom":sQuery(id+"F10.wireOp",EDGE,"E132")}),1.0]])]});
            var Q11;
            Q11=makeQuery(id+"F10.imprint","IMPRINT",FACE,{"disambiguationData":[TD([[makeQuery(id+"F10.imprint","IMPRINT",EDGE,{"derivedFrom":sQuery(id+"F10.wireOp",EDGE,"E124")}),1.0]])]});
            var Q12;
            Q12=makeQuery(id+"F10.imprint","IMPRINT",FACE,{"disambiguationData":[TD([[makeQuery(id+"F10.imprint","IMPRINT",EDGE,{"derivedFrom":sQuery(id+"F10.wireOp",EDGE,"E112")}),1.0]])]});
            var Q13;
            Q13=makeQuery(id+"F10.imprint","IMPRINT",FACE,{"disambiguationData":[TD([[makeQuery(id+"F10.imprint","IMPRINT",EDGE,{"derivedFrom":sQuery(id+"F10.wireOp",EDGE,"E64")}),1.0]])]});
            var Q14;
            Q14=makeQuery(id+"F10.imprint","IMPRINT",FACE,{"disambiguationData":[TD([[makeQuery(id+"F10.imprint","IMPRINT",EDGE,{"derivedFrom":sQuery(id+"F10.wireOp",EDGE,"E68")}),1.0]])]});
            var Q15;
            Q15=makeQuery(id+"F10.imprint","IMPRINT",FACE,{"disambiguationData":[TD([[makeQuery(id+"F10.imprint","IMPRINT",EDGE,{"derivedFrom":sQuery(id+"F10.wireOp",EDGE,"E88")}),1.0]])]});
            var Q16;
            Q16=makeQuery(id+"F10.imprint","IMPRINT",FACE,{"disambiguationData":[TD([[makeQuery(id+"F10.imprint","IMPRINT",EDGE,{"derivedFrom":sQuery(id+"F10.wireOp",EDGE,"E80")}),1.0]])]});
            var Q17;
            Q17=makeQuery(id+"F10.imprint","IMPRINT",FACE,{"disambiguationData":[TD([[makeQuery(id+"F10.imprint","IMPRINT",EDGE,{"derivedFrom":sQuery(id+"F10.wireOp",EDGE,"E32")}),1.0]])]});
            var Q18;
            Q18=makeQuery(id+"F10.imprint","IMPRINT",FACE,{"disambiguationData":[TD([[makeQuery(id+"F10.imprint","IMPRINT",EDGE,{"derivedFrom":sQuery(id+"F10.wireOp",EDGE,"E40")}),1.0]])]});
            var Q19;
            Q19=makeQuery(id+"F10.imprint","IMPRINT",FACE,{"disambiguationData":[TD([[makeQuery(id+"F10.imprint","IMPRINT",EDGE,{"derivedFrom":sQuery(id+"F10.wireOp",EDGE,"E56")}),1.0]])]});
            var Q20;
            Q20=makeQuery(id+"F10.imprint","IMPRINT",FACE,{"disambiguationData":[TD([[makeQuery(id+"F10.imprint","IMPRINT",EDGE,{"derivedFrom":sQuery(id+"F10.wireOp",EDGE,"E96")}),1.0]])]});
            var Q21;
            Q21=makeQuery(id+"F10.imprint","IMPRINT",FACE,{"disambiguationData":[TD([[makeQuery(id+"F10.imprint","IMPRINT",EDGE,{"derivedFrom":sQuery(id+"F10.wireOp",EDGE,"E72")}),1.0]])]});
            var Q22;
            Q22=makeQuery(id+"F10.imprint","IMPRINT",FACE,{"disambiguationData":[TD([[makeQuery(id+"F10.imprint","IMPRINT",EDGE,{"derivedFrom":sQuery(id+"F10.wireOp",EDGE,"E52")}),1.0]])]});
            var Q23;
            Q23=makeQuery(id+"F10.imprint","IMPRINT",FACE,{"disambiguationData":[TD([[makeQuery(id+"F10.imprint","IMPRINT",EDGE,{"derivedFrom":sQuery(id+"F10.wireOp",EDGE,"E92")}),1.0]])]});
            var Q24;
            Q24=makeQuery(id+"F10.imprint","IMPRINT",FACE,{"disambiguationData":[TD([[makeQuery(id+"F10.imprint","IMPRINT",EDGE,{"derivedFrom":sQuery(id+"F10.wireOp",EDGE,"E76")}),1.0]])]});
            var Q25;
            Q25=makeQuery(id+"F10.imprint","IMPRINT",FACE,{"disambiguationData":[TD([[makeQuery(id+"F10.imprint","IMPRINT",EDGE,{"derivedFrom":sQuery(id+"F10.wireOp",EDGE,"E48")}),1.0]])]});
            var Q26;
            Q26=makeQuery(id+"F10.imprint","IMPRINT",FACE,{"disambiguationData":[TD([[makeQuery(id+"F10.imprint","IMPRINT",EDGE,{"derivedFrom":sQuery(id+"F10.wireOp",EDGE,"E136")}),1.0]])]});
            var Q27;
            Q27=makeQuery(id+"F10.imprint","IMPRINT",FACE,{"disambiguationData":[TD([[makeQuery(id+"F10.imprint","IMPRINT",EDGE,{"derivedFrom":sQuery(id+"F10.wireOp",EDGE,"E44")}),1.0]])]});
            var Q28;
            Q28=makeQuery(id+"F10.imprint","IMPRINT",FACE,{"disambiguationData":[TD([[makeQuery(id+"F10.imprint","IMPRINT",EDGE,{"derivedFrom":sQuery(id+"F10.wireOp",EDGE,"E84")}),1.0]])]});
            var Q29;
            Q29=makeQuery(id+"F10.imprint","IMPRINT",FACE,{"disambiguationData":[TD([[makeQuery(id+"F10.imprint","IMPRINT",EDGE,{"derivedFrom":sQuery(id+"F10.wireOp",EDGE,"E28")}),1.0]])]});
            var Q30;
            Q30=makeQuery(id+"F10.imprint","IMPRINT",FACE,{"disambiguationData":[TD([[makeQuery(id+"F10.imprint","IMPRINT",EDGE,{"derivedFrom":sQuery(id+"F10.wireOp",EDGE,"E16")}),1.0]])]});
            var Q31;
            Q31=makeQuery(id+"F10.imprint","IMPRINT",FACE,{"disambiguationData":[TD([[makeQuery(id+"F10.imprint","IMPRINT",EDGE,{"derivedFrom":sQuery(id+"F10.wireOp",EDGE,"E20")}),1.0]])]});
            var Q32;
            Q32=makeQuery(id+"F10.imprint","IMPRINT",FACE,{"disambiguationData":[TD([[makeQuery(id+"F10.imprint","IMPRINT",EDGE,{"derivedFrom":sQuery(id+"F10.wireOp",EDGE,"E36")}),1.0]])]});
            var Q33;
            Q33=makeQuery(id+"F10.imprint","IMPRINT",FACE,{"disambiguationData":[TD([[makeQuery(id+"F10.imprint","IMPRINT",EDGE,{"derivedFrom":sQuery(id+"F10.wireOp",EDGE,"E12")}),-1.0]])]});
            var Q34;
            Q34=makeQuery(id+"F10.imprint","IMPRINT",FACE,{"disambiguationData":[TD([[makeQuery(id+"F10.imprint","IMPRINT",EDGE,{"derivedFrom":sQuery(id+"F10.wireOp",EDGE,"E60")}),1.0]])]});
            var Q35;
            Q35=makeQuery(id+"F10.imprint","IMPRINT",FACE,{"disambiguationData":[TD([[makeQuery(id+"F10.imprint","IMPRINT",EDGE,{"derivedFrom":sQuery(id+"F10.wireOp",EDGE,"E24")}),1.0]])]});
            var Q36;
            Q36=sQuery(id+"F10.wireOp",EDGE,"E197");
            var Q37;
            Q37=sQuery(id+"F10.wireOp",EDGE,"E262");
            var Q38;
            Q38=sQuery(id+"F10.wireOp",EDGE,"E256");
            var Q39;
            Q39=sQuery(id+"F10.wireOp",EDGE,"E263");
            var Q40;
            Q40=sQuery(id+"F10.wireOp",EDGE,"E255");
            var Q41;
            Q41=sQuery(id+"F10.wireOp",EDGE,"E261");
            var Q42;
            Q42=sQuery(id+"F10.wireOp",EDGE,"E254");
            var Q43;
            Q43=sQuery(id+"F10.wireOp",EDGE,"E206");
            var Q44;
            Q44=sQuery(id+"F10.wireOp",EDGE,"E253");
            var Q45;
            Q45=sQuery(id+"F10.wireOp",EDGE,"E232");
            var Q46;
            Q46=sQuery(id+"F10.wireOp",EDGE,"E260");
            var Q47;
            Q47=sQuery(id+"F10.wireOp",EDGE,"E259");
            var Q48;
            Q48=sQuery(id+"F10.wireOp",EDGE,"E258");
            var Q49;
            Q49=sQuery(id+"F10.wireOp",EDGE,"E257");
            var Q50;
            Q50=sQuery(id+"F10.wireOp",EDGE,"E159");
            var Q51;
            Q51=sQuery(id+"F10.wireOp",EDGE,"E188");
            var Q52;
            Q52=sQuery(id+"F10.wireOp",EDGE,"E234");
            var Q53;
            Q53=sQuery(id+"F10.wireOp",EDGE,"E233");
            var Q54;
            Q54=sQuery(id+"F10.wireOp",EDGE,"E235");
            var Q55;
            Q55=sQuery(id+"F10.wireOp",EDGE,"E251");
            var Q56;
            Q56=sQuery(id+"F10.wireOp",EDGE,"E129");
            var Q57;
            Q57=sQuery(id+"F10.wireOp",EDGE,"E161");
            var Q58;
            Q58=sQuery(id+"F10.wireOp",EDGE,"E49");
            var Q59;
            Q59=sQuery(id+"F10.wireOp",EDGE,"E65");
            var Q60;
            Q60=sQuery(id+"F10.wireOp",EDGE,"E69");
            var Q61;
            Q61=sQuery(id+"F10.wireOp",EDGE,"E216");
            var Q62;
            Q62=sQuery(id+"F10.wireOp",EDGE,"E53");
            var Q63;
            Q63=sQuery(id+"F10.wireOp",EDGE,"E37");
            var Q64;
            Q64=sQuery(id+"F10.wireOp",EDGE,"E181");
            var Q65;
            Q65=sQuery(id+"F10.wireOp",EDGE,"E165");
            var Q66;
            Q66=sQuery(id+"F10.wireOp",EDGE,"E229");
            var Q67;
            Q67=sQuery(id+"F10.wireOp",EDGE,"E213");
            var Q68;
            Q68=sQuery(id+"F10.wireOp",EDGE,"E104");
            var Q69;
            Q69=sQuery(id+"F10.wireOp",EDGE,"E40");
            var Q70;
            Q70=sQuery(id+"F10.wireOp",EDGE,"E70");
            var Q71;
            Q71=sQuery(id+"F10.wireOp",EDGE,"E38");
            var Q72;
            Q72=sQuery(id+"F10.wireOp",EDGE,"E250");
            var Q73;
            Q73=sQuery(id+"F10.wireOp",EDGE,"E170");
            var Q74;
            Q74=sQuery(id+"F10.wireOp",EDGE,"E202");
            var Q75;
            Q75=sQuery(id+"F10.wireOp",EDGE,"E118");
            var Q76;
            Q76=sQuery(id+"F10.wireOp",EDGE,"E246");
            var Q77;
            Q77=sQuery(id+"F10.wireOp",EDGE,"E230");
            var Q78;
            Q78=sQuery(id+"F10.wireOp",EDGE,"E214");
            var Q79;
            Q79=sQuery(id+"F10.wireOp",EDGE,"E103");
            var Q80;
            Q80=sQuery(id+"F10.wireOp",EDGE,"E176");
            var Q81;
            Q81=sQuery(id+"F10.wireOp",EDGE,"E71");
            var Q82;
            Q82=sQuery(id+"F10.wireOp",EDGE,"E201");
            var Q83;
            Q83=sQuery(id+"F10.wireOp",EDGE,"E217");
            var Q84;
            Q84=sQuery(id+"F10.wireOp",EDGE,"E39");
            var Q85;
            Q85=sQuery(id+"F10.wireOp",EDGE,"E160");
            var Q86;
            Q86=sQuery(id+"F10.wireOp",EDGE,"E182");
            var Q87;
            Q87=sQuery(id+"F10.wireOp",EDGE,"E198");
            var Q88;
            Q88=sQuery(id+"F10.wireOp",EDGE,"E102");
            var Q89;
            Q89=sQuery(id+"F10.wireOp",EDGE,"E31");
            var Q90;
            Q90=sQuery(id+"F10.wireOp",EDGE,"E119");
            var Q91;
            Q91=sQuery(id+"F10.wireOp",EDGE,"E18");
            var Q92;
            Q92=sQuery(id+"F10.wireOp",EDGE,"E199");
            var Q93;
            Q93=sQuery(id+"F10.wireOp",EDGE,"E183");
            var Q94;
            Q94=sQuery(id+"F10.wireOp",EDGE,"E17");
            var Q95;
            Q95=sQuery(id+"F10.wireOp",EDGE,"E151");
            var Q96;
            Q96=sQuery(id+"F10.wireOp",EDGE,"E247");
            var Q97;
            Q97=sQuery(id+"F10.wireOp",EDGE,"E16");
            var Q98;
            Q98=sQuery(id+"F10.wireOp",EDGE,"E231");
            var Q99;
            Q99=sQuery(id+"F10.wireOp",EDGE,"E215");
            var Q100;
            Q100=sQuery(id+"F10.wireOp",EDGE,"E175");
            var Q101;
            Q101=sQuery(id+"F10.wireOp",EDGE,"E191");
            var Q102;
            Q102=sQuery(id+"F10.wireOp",EDGE,"E207");
            var Q103;
            Q103=sQuery(id+"F10.wireOp",EDGE,"E223");
            var Q104;
            Q104=sQuery(id+"F10.wireOp",EDGE,"E111");
            var Q105;
            Q105=sQuery(id+"F10.wireOp",EDGE,"E127");
            var Q106;
            Q106=sQuery(id+"F10.wireOp",EDGE,"E245");
            var Q107;
            Q107=sQuery(id+"F10.wireOp",EDGE,"E72");
            var Q108;
            Q108=sQuery(id+"F10.wireOp",EDGE,"E174");
            var Q109;
            Q109=sQuery(id+"F10.wireOp",EDGE,"E190");
            var Q110;
            Q110=sQuery(id+"F10.wireOp",EDGE,"E56");
            var Q111;
            Q111=sQuery(id+"F10.wireOp",EDGE,"E222");
            var Q112;
            Q112=sQuery(id+"F10.wireOp",EDGE,"E126");
            var Q113;
            Q113=sQuery(id+"F10.wireOp",EDGE,"E116");
            var Q114;
            Q114=sQuery(id+"F10.wireOp",EDGE,"E36");
            var Q115;
            Q115=sQuery(id+"F10.wireOp",EDGE,"E68");
            var Q116;
            Q116=sQuery(id+"F10.wireOp",EDGE,"E88");
            var Q117;
            Q117=sQuery(id+"F10.wireOp",EDGE,"E200");
            var Q118;
            Q118=sQuery(id+"F10.wireOp",EDGE,"E184");
            var Q119;
            Q119=sQuery(id+"F10.wireOp",EDGE,"E152");
            var Q120;
            Q120=sQuery(id+"F10.wireOp",EDGE,"E173");
            var Q121;
            Q121=sQuery(id+"F10.wireOp",EDGE,"E189");
            var Q122;
            Q122=sQuery(id+"F10.wireOp",EDGE,"E205");
            var Q123;
            Q123=sQuery(id+"F10.wireOp",EDGE,"E221");
            var Q124;
            Q124=sQuery(id+"F10.wireOp",EDGE,"E109");
            var Q125;
            Q125=sQuery(id+"F10.wireOp",EDGE,"E125");
            var Q126;
            Q126=sQuery(id+"F10.wireOp",EDGE,"E141");
            var Q127;
            Q127=sQuery(id+"F10.wireOp",EDGE,"E157");
            var Q128;
            Q128=sQuery(id+"F10.wireOp",EDGE,"E147");
            var Q129;
            Q129=sQuery(id+"F10.wireOp",EDGE,"E163");
            var Q130;
            Q130=sQuery(id+"F10.wireOp",EDGE,"E179");
            var Q131;
            Q131=sQuery(id+"F10.wireOp",EDGE,"E195");
            var Q132;
            Q132=sQuery(id+"F10.wireOp",EDGE,"E99");
            var Q133;
            Q133=sQuery(id+"F10.wireOp",EDGE,"E35");
            var Q134;
            Q134=sQuery(id+"F10.wireOp",EDGE,"E248");
            var Q135;
            Q135=sQuery(id+"F10.wireOp",EDGE,"E108");
            var Q136;
            Q136=sQuery(id+"F10.wireOp",EDGE,"E124");
            var Q137;
            Q137=sQuery(id+"F10.wireOp",EDGE,"E194");
            var Q138;
            Q138=sQuery(id+"F10.wireOp",EDGE,"E210");
            var Q139;
            Q139=sQuery(id+"F10.wireOp",EDGE,"E226");
            var Q140;
            Q140=sQuery(id+"F10.wireOp",EDGE,"E130");
            var Q141;
            Q141=sQuery(id+"F10.wireOp",EDGE,"E146");
            var Q142;
            Q142=sQuery(id+"F10.wireOp",EDGE,"E162");
            var Q143;
            Q143=sQuery(id+"F10.wireOp",EDGE,"E66");
            var Q144;
            Q144=sQuery(id+"F10.wireOp",EDGE,"E212");
            var Q145;
            Q145=sQuery(id+"F10.wireOp",EDGE,"E228");
            var Q146;
            Q146=sQuery(id+"F10.wireOp",EDGE,"E244");
            var Q147;
            Q147=sQuery(id+"F10.wireOp",EDGE,"E164");
            var Q148;
            Q148=sQuery(id+"F10.wireOp",EDGE,"E180");
            var Q149;
            Q149=sQuery(id+"F10.wireOp",EDGE,"E196");
            var Q150;
            Q150=sQuery(id+"F10.wireOp",EDGE,"E211");
            var Q151;
            Q151=sQuery(id+"F10.wireOp",EDGE,"E227");
            var Q152;
            Q152=sQuery(id+"F10.wireOp",EDGE,"E243");
            var Q153;
            Q153=sQuery(id+"F10.wireOp",EDGE,"E67");
            var Q154;
            Q154=sQuery(id+"F10.wireOp",EDGE,"E178");
            var Q155;
            Q155=sQuery(id+"F10.wireOp",EDGE,"E98");
            var Q156;
            Q156=sQuery(id+"F10.wireOp",EDGE,"E34");
            var Q157;
            Q157=sQuery(id+"F10.wireOp",EDGE,"E97");
            var Q158;
            Q158=sQuery(id+"F10.wireOp",EDGE,"E177");
            var Q159;
            Q159=sQuery(id+"F10.wireOp",EDGE,"E193");
            var Q160;
            Q160=sQuery(id+"F10.wireOp",EDGE,"E209");
            var Q161;
            Q161=sQuery(id+"F10.wireOp",EDGE,"E225");
            var Q162;
            Q162=sQuery(id+"F10.wireOp",EDGE,"E64");
            var Q163;
            Q163=sQuery(id+"F10.wireOp",EDGE,"E96");
            var Q164;
            Q164=sQuery(id+"F10.wireOp",EDGE,"E32");
            var Q165;
            Q165=sQuery(id+"F10.wireOp",EDGE,"E192");
            var Q166;
            Q166=sQuery(id+"F10.wireOp",EDGE,"E208");
            var Q167;
            Q167=sQuery(id+"F10.wireOp",EDGE,"E224");
            var Q168;
            Q168=sQuery(id+"F10.wireOp",EDGE,"E143");
            var Q169;
            Q169=sQuery(id+"F10.wireOp",EDGE,"E142");
            var Q170;
            Q170=sQuery(id+"F10.wireOp",EDGE,"E30");
            var Q171;
            Q171=sQuery(id+"F10.wireOp",EDGE,"E237");
            var Q172;
            Q172=sQuery(id+"F10.wireOp",EDGE,"E29");
            var Q173;
            Q173=sQuery(id+"F10.wireOp",EDGE,"E236");
            var Q174;
            Q174=sQuery(id+"F10.wireOp",EDGE,"E252");
            var Q175;
            Q175=sQuery(id+"F10.wireOp",EDGE,"E172");
            var Q176;
            Q176=sQuery(id+"F10.wireOp",EDGE,"E204");
            var Q177;
            Q177=sQuery(id+"F10.wireOp",EDGE,"E220");
            var Q178;
            Q178=sQuery(id+"F10.wireOp",EDGE,"E28");
            var Q179;
            Q179=sQuery(id+"F10.wireOp",EDGE,"E171");
            var Q180;
            Q180=sQuery(id+"F10.wireOp",EDGE,"E187");
            var Q181;
            Q181=sQuery(id+"F10.wireOp",EDGE,"E203");
            var Q182;
            Q182=sQuery(id+"F10.wireOp",EDGE,"E107");
            var Q183;
            Q183=sQuery(id+"F10.wireOp",EDGE,"E139");
            var Q184;
            Q184=sQuery(id+"F10.wireOp",EDGE,"E43");
            var Q185;
            Q185=sQuery(id+"F10.wireOp",EDGE,"E59");
            var Q186;
            Q186=sQuery(id+"F10.wireOp",EDGE,"E75");
            var Q187;
            Q187=sQuery(id+"F10.wireOp",EDGE,"E91");
            var Q188;
            Q188=sQuery(id+"F10.wireOp",EDGE,"E106");
            var Q189;
            Q189=sQuery(id+"F10.wireOp",EDGE,"E138");
            var Q190;
            Q190=sQuery(id+"F10.wireOp",EDGE,"E42");
            var Q191;
            Q191=sQuery(id+"F10.wireOp",EDGE,"E58");
            var Q192;
            Q192=sQuery(id+"F10.wireOp",EDGE,"E74");
            var Q193;
            Q193=sQuery(id+"F10.wireOp",EDGE,"E90");
            var Q194;
            Q194=sQuery(id+"F10.wireOp",EDGE,"E218");
            var Q195;
            Q195=sQuery(id+"F10.wireOp",EDGE,"E41");
            var Q196;
            Q196=sQuery(id+"F10.wireOp",EDGE,"E57");
            var Q197;
            Q197=sQuery(id+"F10.wireOp",EDGE,"E73");
            var Q198;
            Q198=sQuery(id+"F10.wireOp",EDGE,"E89");
            var Q199;
            Q199=sQuery(id+"F10.wireOp",EDGE,"E249");
            var Q200;
            Q200=sQuery(id+"F10.wireOp",EDGE,"E185");
            var Q201;
            Q201=sQuery(id+"F10.wireOp",EDGE,"E137");
            var Q202;
            Q202=sQuery(id+"F10.wireOp",EDGE,"E153");
            var Q203;
            Q203=sQuery(id+"F10.wireOp",EDGE,"E23");
            var Q204;
            Q204=sQuery(id+"F10.wireOp",EDGE,"E22");
            var Q205;
            Q205=sQuery(id+"F10.wireOp",EDGE,"E21");
            var Q206;
            Q206=sQuery(id+"F10.wireOp",EDGE,"E20");
            var Q207;
            Q207=sQuery(id+"F10.wireOp",EDGE,"E19");
            var Q208;
            Q208=sQuery(id+"F10.wireOp",EDGE,"E145");
            var Q209;
            Q209=sQuery(id+"F10.wireOp",EDGE,"E133");
            var Q210;
            Q210=sQuery(id+"F10.wireOp",EDGE,"E117");
            var Q211;
            Q211=sQuery(id+"F10.wireOp",EDGE,"E101");
            var Q212;
            Q212=sQuery(id+"F10.wireOp",EDGE,"E54");
            var Q213;
            Q213=sQuery(id+"F10.wireOp",EDGE,"E186");
            var Q214;
            Q214=sQuery(id+"F10.wireOp",EDGE,"E134");
            var Q215;
            Q215=sQuery(id+"F10.wireOp",EDGE,"E48");
            var Q216;
            Q216=sQuery(id+"F10.wireOp",EDGE,"E105");
            var Q217;
            Q217=sQuery(id+"F10.wireOp",EDGE,"E55");
            var Q218;
            Q218=sQuery(id+"F10.wireOp",EDGE,"E135");
            var Q219;
            Q219=sQuery(id+"F10.wireOp",EDGE,"E150");
            var Q220;
            Q220=sQuery(id+"F10.wireOp",EDGE,"E63");
            var Q221;
            Q221=sQuery(id+"F10.wireOp",EDGE,"E110");
            var Q222;
            Q222=sQuery(id+"F10.wireOp",EDGE,"E136");
            var Q223;
            Q223=sQuery(id+"F10.wireOp",EDGE,"E158");
            var Q224;
            Q224=sQuery(id+"F10.wireOp",EDGE,"E84");
            var Q225;
            Q225=sQuery(id+"F10.wireOp",EDGE,"E100");
            var Q226;
            Q226=sQuery(id+"F10.wireOp",EDGE,"E132");
            var Q227;
            Q227=sQuery(id+"F10.wireOp",EDGE,"E52");
            var Q228;
            Q228=sQuery(id+"F10.wireOp",EDGE,"E140");
            var Q229;
            Q229=sQuery(id+"F10.wireOp",EDGE,"E60");
            var Q230;
            Q230=sQuery(id+"F10.wireOp",EDGE,"E148");
            var Q231;
            Q231=sQuery(id+"F10.wireOp",EDGE,"E51");
            var Q232;
            Q232=sQuery(id+"F10.wireOp",EDGE,"E33");
            var Q233;
            Q233=sQuery(id+"F10.wireOp",EDGE,"E79");
            var Q234;
            Q234=sQuery(id+"F10.wireOp",EDGE,"E95");
            var Q235;
            Q235=sQuery(id+"F10.wireOp",EDGE,"E62");
            var Q236;
            Q236=sQuery(id+"F10.wireOp",EDGE,"E94");
            var Q237;
            Q237=sQuery(id+"F10.wireOp",EDGE,"E76");
            var Q238;
            Q238=sQuery(id+"F10.wireOp",EDGE,"E169");
            var Q239;
            Q239=sQuery(id+"F10.wireOp",EDGE,"E113");
            var Q240;
            Q240=sQuery(id+"F10.wireOp",EDGE,"E81");
            var Q241;
            Q241=sQuery(id+"F10.wireOp",EDGE,"E85");
            var Q242;
            Q242=sQuery(id+"F10.wireOp",EDGE,"E149");
            var Q243;
            Q243=sQuery(id+"F10.wireOp",EDGE,"E86");
            var Q244;
            Q244=sQuery(id+"F10.wireOp",EDGE,"E144");
            var Q245;
            Q245=sQuery(id+"F10.wireOp",EDGE,"E166");
            var Q246;
            Q246=sQuery(id+"F10.wireOp",EDGE,"E87");
            var Q247;
            Q247=sQuery(id+"F10.wireOp",EDGE,"E167");
            var Q248;
            Q248=sQuery(id+"F10.wireOp",EDGE,"E239");
            var Q249;
            Q249=sQuery(id+"F10.wireOp",EDGE,"E238");
            var Q250;
            Q250=sQuery(id+"F10.wireOp",EDGE,"E120");
            var Q251;
            Q251=sQuery(id+"F10.wireOp",EDGE,"E168");
            var Q252;
            Q252=sQuery(id+"F10.wireOp",EDGE,"E61");
            var Q253;
            Q253=sQuery(id+"F10.wireOp",EDGE,"E83");
            var Q254;
            Q254=sQuery(id+"F10.wireOp",EDGE,"E115");
            var Q255;
            Q255=sQuery(id+"F10.wireOp",EDGE,"E131");
            var Q256;
            Q256=sQuery(id+"F10.wireOp",EDGE,"E156");
            var Q257;
            Q257=sQuery(id+"F10.wireOp",EDGE,"E92");
            var Q258;
            Q258=sQuery(id+"F10.wireOp",EDGE,"E114");
            var Q259;
            Q259=sQuery(id+"F10.wireOp",EDGE,"E82");
            var Q260;
            Q260=sQuery(id+"F10.wireOp",EDGE,"E242");
            var Q261;
            Q261=sQuery(id+"F10.wireOp",EDGE,"E241");
            var Q262;
            Q262=sQuery(id+"F10.wireOp",EDGE,"E80");
            var Q263;
            Q263=sQuery(id+"F10.wireOp",EDGE,"E112");
            var Q264;
            Q264=sQuery(id+"F10.wireOp",EDGE,"E128");
            var Q265;
            Q265=sQuery(id+"F10.wireOp",EDGE,"E78");
            var Q266;
            Q266=sQuery(id+"F10.wireOp",EDGE,"E93");
            var Q267;
            Q267=sQuery(id+"F10.wireOp",EDGE,"E219");
            var Q268;
            Q268=sQuery(id+"F10.wireOp",EDGE,"E123");
            var Q269;
            Q269=sQuery(id+"F10.wireOp",EDGE,"E155");
            var Q270;
            Q270=sQuery(id+"F10.wireOp",EDGE,"E122");
            var Q271;
            Q271=sQuery(id+"F10.wireOp",EDGE,"E154");
            var Q272;
            Q272=sQuery(id+"F10.wireOp",EDGE,"E121");
            var Q273;
            Q273=sQuery(id+"F10.wireOp",EDGE,"E24");
            var Q274;
            Q274=sQuery(id+"F10.wireOp",EDGE,"E15");
            var Q275;
            Q275=sQuery(id+"F10.wireOp",EDGE,"E14");
            var Q276;
            Q276=sQuery(id+"F10.wireOp",EDGE,"E13");
            var Q277;
            Q277=sQuery(id+"F10.wireOp",EDGE,"E12");
            var Q278;
            Q278=sQuery(id+"F10.wireOp",EDGE,"E27");
            var Q279;
            Q279=sQuery(id+"F10.wireOp",EDGE,"E26");
            var Q280;
            Q280=sQuery(id+"F10.wireOp",EDGE,"E25");
            var Q281;
            Q281=sQuery(id+"F10.wireOp",EDGE,"E240");
            var Q282;
            Q282=sQuery(id+"F10.wireOp",EDGE,"E46");
            var Q283;
            Q283=sQuery(id+"F10.wireOp",EDGE,"E44");
            var Q284;
            Q284=sQuery(id+"F10.wireOp",EDGE,"E50");
            var Q285;
            Q285=sQuery(id+"F10.wireOp",EDGE,"E47");
            var Q286;
            Q286=sQuery(id+"F10.wireOp",EDGE,"E45");
            var Q287;
            Q287=sQuery(id+"F10.wireOp",EDGE,"E77");
            extrude(context, id + "F11", {"entities" : qUnion([Q0, Q1, Q2, Q3, Q4, Q5, Q6, Q7, Q8, Q9, Q10, Q11, Q12, Q13, Q14, Q15, Q16, Q17, Q18, Q19, Q20, Q21, Q22, Q23, Q24, Q25, Q26, Q27, Q28, Q29, Q30, Q31, Q32, Q33, Q34, Q35]), "operationType" : NewBodyOperationType.REMOVE, "surfaceEntities" : qUnion([Q36, Q37, Q38, Q39, Q40, Q41, Q42, Q43, Q44, Q45, Q46, Q47, Q48, Q49, Q50, Q51, Q52, Q53, Q54, Q55, Q56, Q57, Q58, Q59, Q60, Q61, Q62, Q63, Q64, Q65, Q66, Q67, Q68, Q69, Q70, Q71, Q72, Q73, Q74, Q75, Q76, Q77, Q78, Q79, Q80, Q81, Q82, Q83, Q84, Q85, Q86, Q87, Q88, Q89, Q90, Q91, Q92, Q93, Q94, Q95, Q96, Q97, Q98, Q99, Q100, Q101, Q102, Q103, Q104, Q105, Q106, Q107, Q108, Q109, Q110, Q111, Q112, Q113, Q114, Q115, Q116, Q117, Q118, Q119, Q120, Q121, Q122, Q123, Q124, Q125, Q126, Q127, Q128, Q129, Q130, Q131, Q132, Q133, Q134, Q135, Q136, Q137, Q138, Q139, Q140, Q141, Q142, Q143, Q144, Q145, Q146, Q147, Q148, Q149, Q150, Q151, Q152, Q153, Q154, Q155, Q156, Q157, Q158, Q159, Q160, Q161, Q162, Q163, Q164, Q165, Q166, Q167, Q168, Q169, Q170, Q171, Q172, Q173, Q174, Q175, Q176, Q177, Q178, Q179, Q180, Q181, Q182, Q183, Q184, Q185, Q186, Q187, Q188, Q189, Q190, Q191, Q192, Q193, Q194, Q195, Q196, Q197, Q198, Q199, Q200, Q201, Q202, Q203, Q204, Q205, Q206, Q207, Q208, Q209, Q210, Q211, Q212, Q213, Q214, Q215, Q216, Q217, Q218, Q219, Q220, Q221, Q222, Q223, Q224, Q225, Q226, Q227, Q228, Q229, Q230, Q231, Q232, Q233, Q234, Q235, Q236, Q237, Q238, Q239, Q240, Q241, Q242, Q243, Q244, Q245, Q246, Q247, Q248, Q249, Q250, Q251, Q252, Q253, Q254, Q255, Q256, Q257, Q258, Q259, Q260, Q261, Q262, Q263, Q264, Q265, Q266, Q267, Q268, Q269, Q270, Q271, Q272, Q273, Q274, Q275, Q276, Q277, Q278, Q279, Q280, Q281, Q282, Q283, Q284, Q285, Q286, Q287]), "oppositeDirection" : true, "depth" : 1.5 * mm, "offsetDistance" : 25 * mm});
        }
        {
            var Q0;
            {var subQ0=sQuery(id+"F0.wireOp",EDGE,"E0.right");Q0=makeQuery(id+"F11.boolean.opBoolean","SPLIT",FACE,{"disambiguationData":[TD([makeQuery(id+"F3.opFillet","BLEND_FACE",FACE,{"disambiguationData":[OSD([subQ0])]})])],"derivedFrom":makeQuery(id+"F1.opExtrude","SWEPT_FACE",FACE,{"disambiguationData":[OSD([subQ0])]})});}
            var Q1;
            Q1=makeQuery(id+"F11.boolean.opBoolean","SPLIT",FACE,{"disambiguationData":[TD([makeQuery(id+"F11.opExtrude","SWEPT_FACE",FACE,{"disambiguationData":[OSD([sQuery(id+"F10.wireOp",EDGE,"E256")])]})])],"derivedFrom":makeQuery(id+"F1.opExtrude","SWEPT_FACE",FACE,{"disambiguationData":[OSD([sQuery(id+"F0.wireOp",EDGE,"E0.right")])]})});
            var Q2;
            Q2=makeQuery(id+"F11.boolean.opBoolean","SPLIT",FACE,{"disambiguationData":[TD([makeQuery(id+"F11.opExtrude","SWEPT_FACE",FACE,{"disambiguationData":[OSD([sQuery(id+"F10.wireOp",EDGE,"E210")])]})])],"derivedFrom":makeQuery(id+"F1.opExtrude","SWEPT_FACE",FACE,{"disambiguationData":[OSD([sQuery(id+"F0.wireOp",EDGE,"E0.right")])]})});
            var Q3;
            Q3=makeQuery(id+"F11.boolean.opBoolean","SPLIT",FACE,{"disambiguationData":[TD([makeQuery(id+"F11.opExtrude","SWEPT_FACE",FACE,{"disambiguationData":[OSD([sQuery(id+"F10.wireOp",EDGE,"E260")])]})])],"derivedFrom":makeQuery(id+"F1.opExtrude","SWEPT_FACE",FACE,{"disambiguationData":[OSD([sQuery(id+"F0.wireOp",EDGE,"E0.right")])]})});
            var Q4;
            Q4=makeQuery(id+"F11.boolean.opBoolean","COPY",FACE,{"derivedFrom":makeQuery(id+"F11.opExtrude","CAP_FACE",FACE,{"disambiguationData":[OSD([sQuery(id+"F10.wireOp",EDGE,"E152"),sQuery(id+"F10.wireOp",EDGE,"E153"),sQuery(id+"F10.wireOp",EDGE,"E154"),sQuery(id+"F10.wireOp",EDGE,"E155"),sQuery(id+"F10.wireOp",EDGE,"E156"),sQuery(id+"F10.wireOp",EDGE,"E157"),sQuery(id+"F10.wireOp",EDGE,"E158"),sQuery(id+"F10.wireOp",EDGE,"E159"),sQuery(id+"F10.wireOp",EDGE,"E160"),sQuery(id+"F10.wireOp",EDGE,"E161"),sQuery(id+"F10.wireOp",EDGE,"E162"),sQuery(id+"F10.wireOp",EDGE,"E163"),sQuery(id+"F10.wireOp",EDGE,"E164"),sQuery(id+"F10.wireOp",EDGE,"E165"),sQuery(id+"F10.wireOp",EDGE,"E166"),sQuery(id+"F10.wireOp",EDGE,"E167"),sQuery(id+"F10.wireOp",EDGE,"E168"),sQuery(id+"F10.wireOp",EDGE,"E169"),sQuery(id+"F10.wireOp",EDGE,"E170"),sQuery(id+"F10.wireOp",EDGE,"E171"),sQuery(id+"F10.wireOp",EDGE,"E172"),sQuery(id+"F10.wireOp",EDGE,"E173"),sQuery(id+"F10.wireOp",EDGE,"E174"),sQuery(id+"F10.wireOp",EDGE,"E175"),sQuery(id+"F10.wireOp",EDGE,"E176"),sQuery(id+"F10.wireOp",EDGE,"E177"),sQuery(id+"F10.wireOp",EDGE,"E178"),sQuery(id+"F10.wireOp",EDGE,"E179"),sQuery(id+"F10.wireOp",EDGE,"E180"),sQuery(id+"F10.wireOp",EDGE,"E181"),sQuery(id+"F10.wireOp",EDGE,"E182"),sQuery(id+"F10.wireOp",EDGE,"E183"),sQuery(id+"F10.wireOp",EDGE,"E184"),sQuery(id+"F10.wireOp",EDGE,"E185"),sQuery(id+"F10.wireOp",EDGE,"E186"),sQuery(id+"F10.wireOp",EDGE,"E187"),sQuery(id+"F10.wireOp",EDGE,"E188"),sQuery(id+"F10.wireOp",EDGE,"E189"),sQuery(id+"F10.wireOp",EDGE,"E190"),sQuery(id+"F10.wireOp",EDGE,"E191"),sQuery(id+"F10.wireOp",EDGE,"E192"),sQuery(id+"F10.wireOp",EDGE,"E193"),sQuery(id+"F10.wireOp",EDGE,"E194"),sQuery(id+"F10.wireOp",EDGE,"E195"),sQuery(id+"F10.wireOp",EDGE,"E196"),sQuery(id+"F10.wireOp",EDGE,"E197"),sQuery(id+"F10.wireOp",EDGE,"E198"),sQuery(id+"F10.wireOp",EDGE,"E199"),sQuery(id+"F10.wireOp",EDGE,"E200"),sQuery(id+"F10.wireOp",EDGE,"E201"),sQuery(id+"F10.wireOp",EDGE,"E202"),sQuery(id+"F10.wireOp",EDGE,"E203"),sQuery(id+"F10.wireOp",EDGE,"E204"),sQuery(id+"F10.wireOp",EDGE,"E205"),sQuery(id+"F10.wireOp",EDGE,"E206"),sQuery(id+"F10.wireOp",EDGE,"E207"),sQuery(id+"F10.wireOp",EDGE,"E208"),sQuery(id+"F10.wireOp",EDGE,"E209"),sQuery(id+"F10.wireOp",EDGE,"E210"),sQuery(id+"F10.wireOp",EDGE,"E211"),sQuery(id+"F10.wireOp",EDGE,"E212"),sQuery(id+"F10.wireOp",EDGE,"E213"),sQuery(id+"F10.wireOp",EDGE,"E214"),sQuery(id+"F10.wireOp",EDGE,"E215"),sQuery(id+"F10.wireOp",EDGE,"E216"),sQuery(id+"F10.wireOp",EDGE,"E217"),sQuery(id+"F10.wireOp",EDGE,"E218"),sQuery(id+"F10.wireOp",EDGE,"E219"),sQuery(id+"F10.wireOp",EDGE,"E220"),sQuery(id+"F10.wireOp",EDGE,"E221"),sQuery(id+"F10.wireOp",EDGE,"E222"),sQuery(id+"F10.wireOp",EDGE,"E223"),sQuery(id+"F10.wireOp",EDGE,"E224"),sQuery(id+"F10.wireOp",EDGE,"E225"),sQuery(id+"F10.wireOp",EDGE,"E226"),sQuery(id+"F10.wireOp",EDGE,"E227"),sQuery(id+"F10.wireOp",EDGE,"E228"),sQuery(id+"F10.wireOp",EDGE,"E229"),sQuery(id+"F10.wireOp",EDGE,"E230"),sQuery(id+"F10.wireOp",EDGE,"E231"),sQuery(id+"F10.wireOp",EDGE,"E232"),sQuery(id+"F10.wireOp",EDGE,"E233"),sQuery(id+"F10.wireOp",EDGE,"E234"),sQuery(id+"F10.wireOp",EDGE,"E235"),sQuery(id+"F10.wireOp",EDGE,"E236"),sQuery(id+"F10.wireOp",EDGE,"E237"),sQuery(id+"F10.wireOp",EDGE,"E238"),sQuery(id+"F10.wireOp",EDGE,"E239"),sQuery(id+"F10.wireOp",EDGE,"E240"),sQuery(id+"F10.wireOp",EDGE,"E241"),sQuery(id+"F10.wireOp",EDGE,"E242"),sQuery(id+"F10.wireOp",EDGE,"E243"),sQuery(id+"F10.wireOp",EDGE,"E244"),sQuery(id+"F10.wireOp",EDGE,"E245"),sQuery(id+"F10.wireOp",EDGE,"E246"),sQuery(id+"F10.wireOp",EDGE,"E247"),sQuery(id+"F10.wireOp",EDGE,"E248"),sQuery(id+"F10.wireOp",EDGE,"E249"),sQuery(id+"F10.wireOp",EDGE,"E250"),sQuery(id+"F10.wireOp",EDGE,"E251"),sQuery(id+"F10.wireOp",EDGE,"E252"),sQuery(id+"F10.wireOp",EDGE,"E253"),sQuery(id+"F10.wireOp",EDGE,"E254"),sQuery(id+"F10.wireOp",EDGE,"E255"),sQuery(id+"F10.wireOp",EDGE,"E256"),sQuery(id+"F10.wireOp",EDGE,"E257"),sQuery(id+"F10.wireOp",EDGE,"E258"),sQuery(id+"F10.wireOp",EDGE,"E259"),sQuery(id+"F10.wireOp",EDGE,"E260"),sQuery(id+"F10.wireOp",EDGE,"E261"),sQuery(id+"F10.wireOp",EDGE,"E262"),sQuery(id+"F10.wireOp",EDGE,"E263")])],"isStart":false})});
            fillet(context, id + "F12", {"entities" : qUnion([Q0, Q1, Q2, Q3, Q4]), "radius" : 0.04 * mm, "tangentPropagation" : true, "allowEdgeOverflow" : false});
        }
        {
            var Q0;
            Q0=qCreatedBy(makeId("Right.planeOp"),FACE);
            var sketch = newSketch(context, id + "F13", { "sketchPlane" : qUnion([Q0])});
            skLineSegment(sketch, "E264", {"start": v(0, 0) * mm, "end": v(0, 54.81) * mm});
            skSolve(sketch);
        }
        {
            var Q0;
            Q0=makeQuery(id+"F1.opExtrude","CAP_FACE",FACE,{"disambiguationData":[OSD([sQuery(id+"F0.wireOp",EDGE,"E0.bottom"),sQuery(id+"F0.wireOp",EDGE,"E0.top"),sQuery(id+"F0.wireOp",EDGE,"E0.left"),sQuery(id+"F0.wireOp",EDGE,"E0.right")])],"isStart":true});
            var sketch = newSketch(context, id + "F14", { "sketchPlane" : qUnion([Q0])});
            skSolve(sketch);
        }
        {
            var Q0;
            {var subQ0=sQuery(id+"F0.wireOp",EDGE,"E0.right");var subQ1=sQuery(id+"F0.wireOp",EDGE,"E0.left");var subQ2=sQuery(id+"F0.wireOp",EDGE,"E0.top");var subQ3=sQuery(id+"F0.wireOp",EDGE,"E0.bottom");var subQ4=makeQuery(id+"F1.opExtrude","CAP_FACE",FACE,{"disambiguationData":[OSD([subQ3,subQ2,subQ1,subQ0])],"isStart":true});Q0=makeQuery(id+"F14.imprint","IMPRINT",FACE,{"disambiguationData":[TD([[makeQuery(id+"F14.imprint","IMPRINT",EDGE,{"derivedFrom":makeQuery(id+"F3.opFillet","BLEND_EDGE",EDGE,{"blendedFrom":[makeQuery(id+"F1.opExtrude","CAP_EDGE",EDGE,{"disambiguationData":[OSD([subQ3])],"isStart":true}),subQ4],"blendedInto":[subQ4]})}),1.0]])]});}
            extrude(context, id + "F15", {"entities" : qUnion([Q0]), "operationType" : NewBodyOperationType.ADD, "depth" : 3 * mm, "offsetDistance" : 25 * mm});
        }
        {
            var Q0;
            {var subQ0=sQuery(id+"F0.wireOp",EDGE,"E0.right");var subQ1=sQuery(id+"F0.wireOp",EDGE,"E0.left");var subQ2=sQuery(id+"F0.wireOp",EDGE,"E0.top");var subQ3=sQuery(id+"F0.wireOp",EDGE,"E0.bottom");var subQ4=makeQuery(id+"F1.opExtrude","CAP_FACE",FACE,{"disambiguationData":[OSD([subQ3,subQ2,subQ1,subQ0])],"isStart":true});Q0=makeQuery(id+"F15.opExtrude","SWEPT_EDGE",EDGE,{"disambiguationData":[OSD([subQ3,subQ2,subQ1,subQ0]),TDD([makeQuery(id+"F14.imprint","INTERSECT",VERTEX,{"derivedFrom":[makeQuery(id+"F3.opFillet","BLEND_EDGE",EDGE,{"blendedFrom":[makeQuery(id+"F1.opExtrude","CAP_EDGE",EDGE,{"disambiguationData":[OSD([subQ2])],"isStart":true}),subQ4],"blendedInto":[subQ4]}),makeQuery(id+"F3.opFillet","BLEND_EDGE",EDGE,{"blendedFrom":[makeQuery(id+"F1.opExtrude","CAP_EDGE",EDGE,{"disambiguationData":[OSD([subQ0])],"isStart":true}),subQ4],"blendedInto":[subQ4]})]})])]});}
            var Q1;
            {var subQ0=sQuery(id+"F0.wireOp",EDGE,"E0.right");var subQ1=sQuery(id+"F0.wireOp",EDGE,"E0.left");var subQ2=sQuery(id+"F0.wireOp",EDGE,"E0.top");var subQ3=sQuery(id+"F0.wireOp",EDGE,"E0.bottom");var subQ4=makeQuery(id+"F1.opExtrude","CAP_FACE",FACE,{"disambiguationData":[OSD([subQ3,subQ2,subQ1,subQ0])],"isStart":true});Q1=makeQuery(id+"F15.opExtrude","SWEPT_EDGE",EDGE,{"disambiguationData":[OSD([subQ3,subQ2,subQ1,subQ0]),TDD([makeQuery(id+"F14.imprint","INTERSECT",VERTEX,{"derivedFrom":[makeQuery(id+"F3.opFillet","BLEND_EDGE",EDGE,{"blendedFrom":[makeQuery(id+"F1.opExtrude","CAP_EDGE",EDGE,{"disambiguationData":[OSD([subQ2])],"isStart":true}),subQ4],"blendedInto":[subQ4]}),makeQuery(id+"F3.opFillet","BLEND_EDGE",EDGE,{"blendedFrom":[makeQuery(id+"F1.opExtrude","CAP_EDGE",EDGE,{"disambiguationData":[OSD([subQ1])],"isStart":true}),subQ4],"blendedInto":[subQ4]})]})])]});}
            var Q2;
            {var subQ0=sQuery(id+"F0.wireOp",EDGE,"E0.right");var subQ1=sQuery(id+"F0.wireOp",EDGE,"E0.left");var subQ2=sQuery(id+"F0.wireOp",EDGE,"E0.top");var subQ3=sQuery(id+"F0.wireOp",EDGE,"E0.bottom");var subQ4=makeQuery(id+"F1.opExtrude","CAP_FACE",FACE,{"disambiguationData":[OSD([subQ3,subQ2,subQ1,subQ0])],"isStart":true});Q2=makeQuery(id+"F15.opExtrude","SWEPT_EDGE",EDGE,{"disambiguationData":[OSD([subQ3,subQ2,subQ1,subQ0]),TDD([makeQuery(id+"F14.imprint","INTERSECT",VERTEX,{"derivedFrom":[makeQuery(id+"F3.opFillet","BLEND_EDGE",EDGE,{"blendedFrom":[makeQuery(id+"F1.opExtrude","CAP_EDGE",EDGE,{"disambiguationData":[OSD([subQ3])],"isStart":true}),subQ4],"blendedInto":[subQ4]}),makeQuery(id+"F3.opFillet","BLEND_EDGE",EDGE,{"blendedFrom":[makeQuery(id+"F1.opExtrude","CAP_EDGE",EDGE,{"disambiguationData":[OSD([subQ1])],"isStart":true}),subQ4],"blendedInto":[subQ4]})]})])]});}
            var Q3;
            {var subQ0=sQuery(id+"F0.wireOp",EDGE,"E0.right");var subQ1=sQuery(id+"F0.wireOp",EDGE,"E0.left");var subQ2=sQuery(id+"F0.wireOp",EDGE,"E0.top");var subQ3=sQuery(id+"F0.wireOp",EDGE,"E0.bottom");var subQ4=makeQuery(id+"F1.opExtrude","CAP_FACE",FACE,{"disambiguationData":[OSD([subQ3,subQ2,subQ1,subQ0])],"isStart":true});Q3=makeQuery(id+"F15.opExtrude","SWEPT_EDGE",EDGE,{"disambiguationData":[OSD([subQ3,subQ2,subQ1,subQ0]),TDD([makeQuery(id+"F14.imprint","INTERSECT",VERTEX,{"derivedFrom":[makeQuery(id+"F3.opFillet","BLEND_EDGE",EDGE,{"blendedFrom":[makeQuery(id+"F1.opExtrude","CAP_EDGE",EDGE,{"disambiguationData":[OSD([subQ3])],"isStart":true}),subQ4],"blendedInto":[subQ4]}),makeQuery(id+"F3.opFillet","BLEND_EDGE",EDGE,{"blendedFrom":[makeQuery(id+"F1.opExtrude","CAP_EDGE",EDGE,{"disambiguationData":[OSD([subQ0])],"isStart":true}),subQ4],"blendedInto":[subQ4]})]})])]});}
            fillet(context, id + "F16", {"entities" : qUnion([Q0, Q1, Q2, Q3]), "radius" : 5 * mm, "tangentPropagation" : true, "allowEdgeOverflow" : false});
        }
        {
            var Q0;
            {var subQ0=sQuery(id+"F0.wireOp",EDGE,"E0.top");var subQ1=sQuery(id+"F0.wireOp",EDGE,"E0.right");var subQ2=sQuery(id+"F0.wireOp",EDGE,"E0.left");var subQ3=sQuery(id+"F0.wireOp",EDGE,"E0.bottom");var subQ4=makeQuery(id+"F1.opExtrude","CAP_FACE",FACE,{"disambiguationData":[OSD([subQ3,subQ0,subQ2,subQ1])],"isStart":true});Q0=makeQuery(id+"F16.opFillet","BLEND_EDGE",EDGE,{"blendedFrom":[makeQuery(id+"F15.opExtrude","SWEPT_EDGE",EDGE,{"disambiguationData":[OSD([subQ3,subQ0,subQ2,subQ1]),TDD([makeQuery(id+"F14.imprint","INTERSECT",VERTEX,{"derivedFrom":[makeQuery(id+"F3.opFillet","BLEND_EDGE",EDGE,{"blendedFrom":[makeQuery(id+"F1.opExtrude","CAP_EDGE",EDGE,{"disambiguationData":[OSD([subQ0])],"isStart":true}),subQ4],"blendedInto":[subQ4]}),makeQuery(id+"F3.opFillet","BLEND_EDGE",EDGE,{"blendedFrom":[makeQuery(id+"F1.opExtrude","CAP_EDGE",EDGE,{"disambiguationData":[OSD([subQ2])],"isStart":true}),subQ4],"blendedInto":[subQ4]})]})])]}),makeQuery(id+"F3.opFillet","BLEND_FACE",FACE,{"disambiguationData":[OSD([subQ0])]})],"blendedInto":[makeQuery(id+"F3.opFillet","BLEND_FACE",FACE,{"disambiguationData":[OSD([subQ0])]})]});}
            var Q1;
            {var subQ0=sQuery(id+"F0.wireOp",EDGE,"E0.right");var subQ1=sQuery(id+"F0.wireOp",EDGE,"E0.left");var subQ2=sQuery(id+"F0.wireOp",EDGE,"E0.top");var subQ3=sQuery(id+"F0.wireOp",EDGE,"E0.bottom");var subQ4=makeQuery(id+"F3.opFillet","BLEND_EDGE",EDGE,{"blendedFrom":[makeQuery(id+"F1.opExtrude","CAP_EDGE",EDGE,{"disambiguationData":[OSD([subQ1])],"isStart":true}),makeQuery(id+"F1.opExtrude","CAP_FACE",FACE,{"disambiguationData":[OSD([subQ3,subQ2,subQ1,subQ0])],"isStart":true})],"blendedInto":[makeQuery(id+"F1.opExtrude","CAP_FACE",FACE,{"disambiguationData":[OSD([subQ3,subQ2,subQ1,subQ0])],"isStart":true})]});Q1=makeQuery(id+"F15.boolean.opBoolean","MERGE",EDGE,{"derivedFrom":[subQ4,makeQuery(id+"F15.opExtrude","CAP_EDGE",EDGE,{"disambiguationData":[OSD([subQ3,subQ2,subQ1,subQ0]),TDD([makeQuery(id+"F14.imprint","IMPRINT",EDGE,{"derivedFrom":subQ4})])],"isStart":true})]});}
            var Q2;
            {var subQ0=sQuery(id+"F0.wireOp",EDGE,"E0.right");var subQ1=sQuery(id+"F0.wireOp",EDGE,"E0.left");var subQ2=sQuery(id+"F0.wireOp",EDGE,"E0.top");var subQ3=sQuery(id+"F0.wireOp",EDGE,"E0.bottom");var subQ4=makeQuery(id+"F3.opFillet","BLEND_EDGE",EDGE,{"blendedFrom":[makeQuery(id+"F1.opExtrude","CAP_EDGE",EDGE,{"disambiguationData":[OSD([subQ3])],"isStart":true}),makeQuery(id+"F1.opExtrude","CAP_FACE",FACE,{"disambiguationData":[OSD([subQ3,subQ2,subQ1,subQ0])],"isStart":true})],"blendedInto":[makeQuery(id+"F1.opExtrude","CAP_FACE",FACE,{"disambiguationData":[OSD([subQ3,subQ2,subQ1,subQ0])],"isStart":true})]});Q2=makeQuery(id+"F15.boolean.opBoolean","MERGE",EDGE,{"derivedFrom":[subQ4,makeQuery(id+"F15.opExtrude","CAP_EDGE",EDGE,{"disambiguationData":[OSD([subQ3,subQ2,subQ1,subQ0]),TDD([makeQuery(id+"F14.imprint","IMPRINT",EDGE,{"derivedFrom":subQ4})])],"isStart":true})]});}
            var Q3;
            {var subQ0=sQuery(id+"F0.wireOp",EDGE,"E0.right");var subQ1=sQuery(id+"F0.wireOp",EDGE,"E0.left");var subQ2=sQuery(id+"F0.wireOp",EDGE,"E0.top");var subQ3=sQuery(id+"F0.wireOp",EDGE,"E0.bottom");var subQ4=makeQuery(id+"F3.opFillet","BLEND_EDGE",EDGE,{"blendedFrom":[makeQuery(id+"F1.opExtrude","CAP_EDGE",EDGE,{"disambiguationData":[OSD([subQ0])],"isStart":true}),makeQuery(id+"F1.opExtrude","CAP_FACE",FACE,{"disambiguationData":[OSD([subQ3,subQ2,subQ1,subQ0])],"isStart":true})],"blendedInto":[makeQuery(id+"F1.opExtrude","CAP_FACE",FACE,{"disambiguationData":[OSD([subQ3,subQ2,subQ1,subQ0])],"isStart":true})]});Q3=makeQuery(id+"F15.boolean.opBoolean","MERGE",EDGE,{"derivedFrom":[subQ4,makeQuery(id+"F15.opExtrude","CAP_EDGE",EDGE,{"disambiguationData":[OSD([subQ3,subQ2,subQ1,subQ0]),TDD([makeQuery(id+"F14.imprint","IMPRINT",EDGE,{"derivedFrom":subQ4})])],"isStart":true})]});}
            var Q4;
            {var subQ0=sQuery(id+"F0.wireOp",EDGE,"E0.right");var subQ1=sQuery(id+"F0.wireOp",EDGE,"E0.left");var subQ2=sQuery(id+"F0.wireOp",EDGE,"E0.top");var subQ3=sQuery(id+"F0.wireOp",EDGE,"E0.bottom");var subQ4=makeQuery(id+"F1.opExtrude","CAP_FACE",FACE,{"disambiguationData":[OSD([subQ3,subQ2,subQ1,subQ0])],"isStart":true});Q4=makeQuery(id+"F16.opFillet","BLEND_EDGE",EDGE,{"blendedFrom":[makeQuery(id+"F15.opExtrude","SWEPT_EDGE",EDGE,{"disambiguationData":[OSD([subQ3,subQ2,subQ1,subQ0]),TDD([makeQuery(id+"F14.imprint","INTERSECT",VERTEX,{"derivedFrom":[makeQuery(id+"F3.opFillet","BLEND_EDGE",EDGE,{"blendedFrom":[makeQuery(id+"F1.opExtrude","CAP_EDGE",EDGE,{"disambiguationData":[OSD([subQ3])],"isStart":true}),subQ4],"blendedInto":[subQ4]}),makeQuery(id+"F3.opFillet","BLEND_EDGE",EDGE,{"blendedFrom":[makeQuery(id+"F1.opExtrude","CAP_EDGE",EDGE,{"disambiguationData":[OSD([subQ0])],"isStart":true}),subQ4],"blendedInto":[subQ4]})]})])]}),makeQuery(id+"F15.opExtrude","CAP_FACE",FACE,{"disambiguationData":[OSD([subQ3,subQ2,subQ1,subQ0])],"isStart":false})],"blendedInto":[makeQuery(id+"F15.opExtrude","CAP_FACE",FACE,{"disambiguationData":[OSD([subQ3,subQ2,subQ1,subQ0])],"isStart":false})]});}
            var Q5;
            {var subQ0=sQuery(id+"F0.wireOp",EDGE,"E0.right");var subQ1=sQuery(id+"F0.wireOp",EDGE,"E0.left");var subQ2=sQuery(id+"F0.wireOp",EDGE,"E0.top");var subQ3=sQuery(id+"F0.wireOp",EDGE,"E0.bottom");var subQ4=makeQuery(id+"F1.opExtrude","CAP_FACE",FACE,{"disambiguationData":[OSD([subQ3,subQ2,subQ1,subQ0])],"isStart":true});Q5=makeQuery(id+"F16.opFillet","BLEND_EDGE",EDGE,{"blendedFrom":[makeQuery(id+"F15.opExtrude","SWEPT_EDGE",EDGE,{"disambiguationData":[OSD([subQ3,subQ2,subQ1,subQ0]),TDD([makeQuery(id+"F14.imprint","INTERSECT",VERTEX,{"derivedFrom":[makeQuery(id+"F3.opFillet","BLEND_EDGE",EDGE,{"blendedFrom":[makeQuery(id+"F1.opExtrude","CAP_EDGE",EDGE,{"disambiguationData":[OSD([subQ2])],"isStart":true}),subQ4],"blendedInto":[subQ4]}),makeQuery(id+"F3.opFillet","BLEND_EDGE",EDGE,{"blendedFrom":[makeQuery(id+"F1.opExtrude","CAP_EDGE",EDGE,{"disambiguationData":[OSD([subQ0])],"isStart":true}),subQ4],"blendedInto":[subQ4]})]})])]}),makeQuery(id+"F15.opExtrude","CAP_FACE",FACE,{"disambiguationData":[OSD([subQ3,subQ2,subQ1,subQ0])],"isStart":false})],"blendedInto":[makeQuery(id+"F15.opExtrude","CAP_FACE",FACE,{"disambiguationData":[OSD([subQ3,subQ2,subQ1,subQ0])],"isStart":false})]});}
            fillet(context, id + "F17", {"entities" : qUnion([Q0, Q1, Q2, Q3, Q4, Q5]), "radius" : 1.5 * mm, "tangentPropagation" : true, "allowEdgeOverflow" : false});
        }
    });
